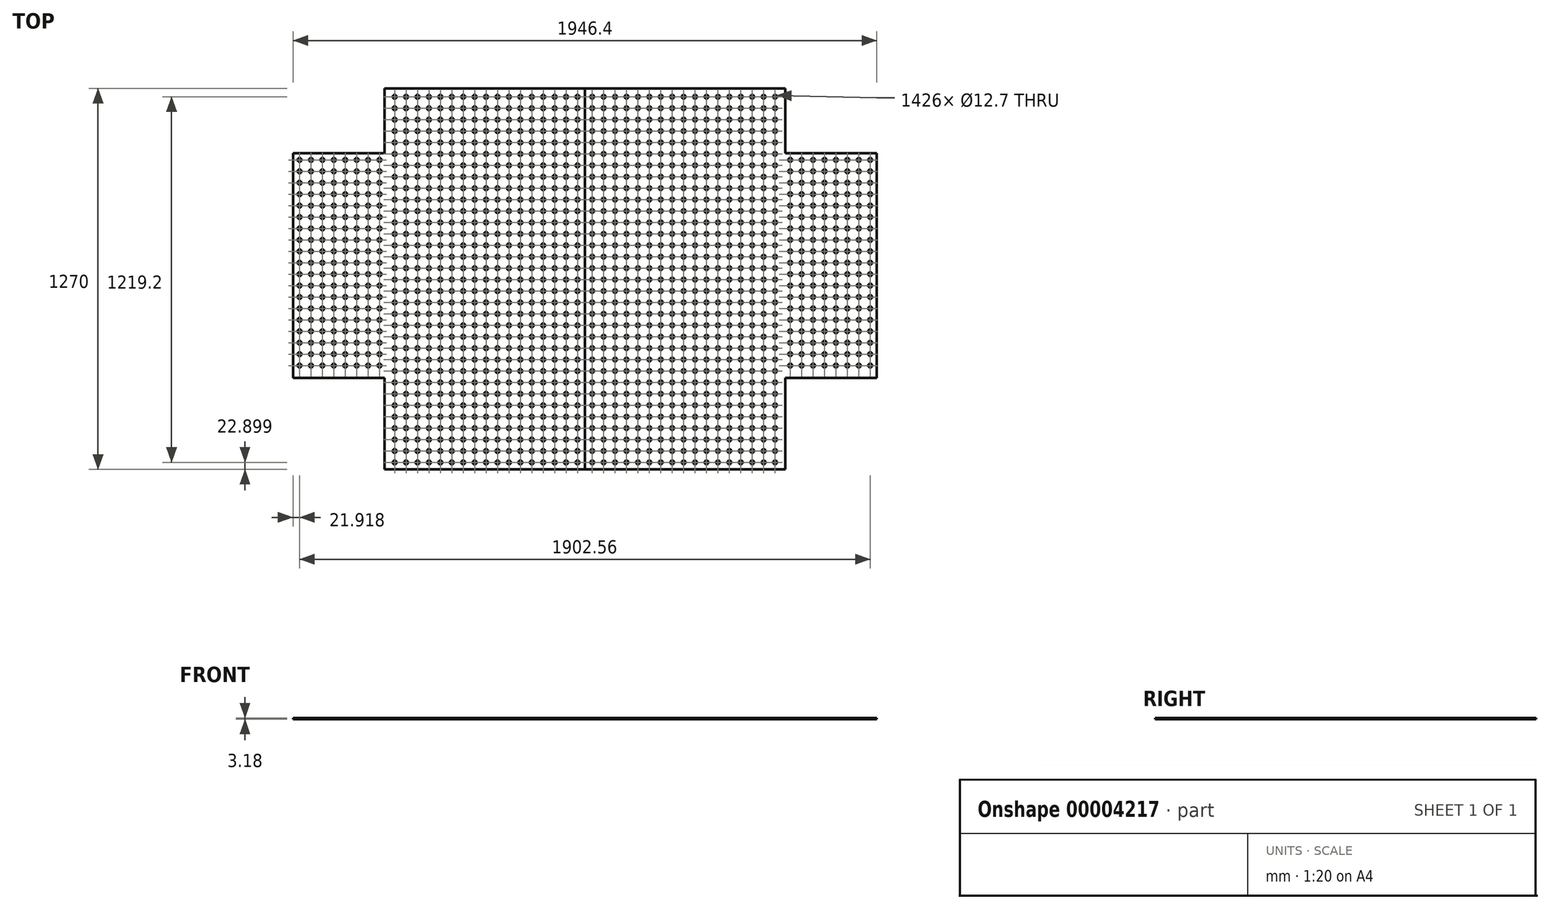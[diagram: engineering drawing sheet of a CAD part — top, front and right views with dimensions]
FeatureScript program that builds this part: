
annotation { "Feature Type Name" : "Feature", "Feature Type Description" : "" }
export const myFeature = defineFeature(function(context is Context, id is Id, definition is map)
    precondition{}
    {
        {
            var Q0;
            Q0=qCreatedBy(makeId("Top.planeOp"),FACE);
            var sketch = newSketch(context, id + "F0", { "sketchPlane" : qUnion([Q0])});
            skLineSegment(sketch, "E0.rect.bottom", {"start": v(-668.4, 635) * mm, "end": v(668.4, 635) * mm});
            skLineSegment(sketch, "E0.rect.top", {"start": v(-668.4, -635) * mm, "end": v(668.4, -635) * mm});
            skLineSegment(sketch, "E0.rect.left", {"start": v(-973.2, 419.1) * mm, "end": v(-973.2, -330.2) * mm});
            skLineSegment(sketch, "E0.rect.right", {"start": v(973.2, 419.1) * mm, "end": v(973.2, -330.2) * mm});
            skPoint(sketch, "E0.rect.middle", {"position": v(0, 0) * mm});
            skLineSegment(sketch, "E1.0", {"start": v(-973.2, 419.1) * mm, "end": v(-668.4, 419.1) * mm});
            skLineSegment(sketch, "E2.0", {"start": v(-973.2, -330.2) * mm, "end": v(-668.4, -330.2) * mm});
            skLineSegment(sketch, "E3.0", {"start": v(668.4, 635) * mm, "end": v(668.4, 419.1) * mm});
            skLineSegment(sketch, "E4.0", {"start": v(-668.4, 635) * mm, "end": v(-668.4, 419.1) * mm});
            skLineSegment(sketch, "E5.trimOffspring", {"start": v(668.4, 419.1) * mm, "end": v(973.2, 419.1) * mm});
            skLineSegment(sketch, "E6.trimOffspring", {"start": v(-668.4, -330.2) * mm, "end": v(-668.4, -635) * mm});
            skLineSegment(sketch, "E7.trimOffspring", {"start": v(668.4, -330.2) * mm, "end": v(973.2, -330.2) * mm});
            skLineSegment(sketch, "E8.trimOffspring", {"start": v(668.4, -330.2) * mm, "end": v(668.4, -635) * mm});
            skPoint(sketch, "E9.orphan", {"position": v(973.2, 635) * mm});
            skPoint(sketch, "E10.orphan", {"position": v(973.2, -635) * mm});
            skPoint(sketch, "E11.orphan", {"position": v(-973.2, -635) * mm});
            skPoint(sketch, "E12.orphan", {"position": v(-973.2, 635) * mm});
            skSolve(sketch);
        }
        {
            var Q0;
            Q0 = qSketchRegion(id + "F0", true);
            extrude(context, id + "F1", {"entities" : qUnion([Q0]), "depth" : 3.17 * mm});
        }
        {
            var Q0;
            Q0=makeQuery(id+"F1.opExtrude","CAP_FACE",FACE,{"disambiguationData":[OSD([sQuery(id+"F0.wireOp",EDGE,"E0.rect.bottom"),sQuery(id+"F0.wireOp",EDGE,"E0.rect.top"),sQuery(id+"F0.wireOp",EDGE,"E0.rect.left"),sQuery(id+"F0.wireOp",EDGE,"E0.rect.right"),sQuery(id+"F0.wireOp",EDGE,"E1.0"),sQuery(id+"F0.wireOp",EDGE,"E2.0"),sQuery(id+"F0.wireOp",EDGE,"E3.0"),sQuery(id+"F0.wireOp",EDGE,"E4.0"),sQuery(id+"F0.wireOp",EDGE,"E5.trimOffspring"),sQuery(id+"F0.wireOp",EDGE,"E6.trimOffspring"),sQuery(id+"F0.wireOp",EDGE,"E7.trimOffspring"),sQuery(id+"F0.wireOp",EDGE,"E8.trimOffspring")])],"isStart":false});
            var sketch = newSketch(context, id + "F2", { "sketchPlane" : qUnion([Q0])});
            skCircle(sketch, "E13", {"center": v(-634.04, 607.1) * mm, "radius": 6.35 * mm});
            skCircle(sketch, "E14.0.1.0", {"center": v(-634.04, 569) * mm, "radius": 6.35 * mm});
            skCircle(sketch, "E14.0.2.0", {"center": v(-634.04, 530.9) * mm, "radius": 6.35 * mm});
            skCircle(sketch, "E14.0.3.0", {"center": v(-634.04, 492.8) * mm, "radius": 6.35 * mm});
            skCircle(sketch, "E14.0.4.0", {"center": v(-634.04, 454.7) * mm, "radius": 6.35 * mm});
            skCircle(sketch, "E14.0.5.0", {"center": v(-634.04, 416.6) * mm, "radius": 6.35 * mm});
            skCircle(sketch, "E14.0.6.0", {"center": v(-634.04, 378.5) * mm, "radius": 6.35 * mm});
            skCircle(sketch, "E14.0.7.0", {"center": v(-634.04, 340.4) * mm, "radius": 6.35 * mm});
            skCircle(sketch, "E14.0.8.0", {"center": v(-634.04, 302.3) * mm, "radius": 6.35 * mm});
            skCircle(sketch, "E14.0.9.0", {"center": v(-634.04, 264.2) * mm, "radius": 6.35 * mm});
            skCircle(sketch, "E14.0.10.0", {"center": v(-634.04, 226.1) * mm, "radius": 6.35 * mm});
            skCircle(sketch, "E14.0.11.0", {"center": v(-634.04, 188) * mm, "radius": 6.35 * mm});
            skCircle(sketch, "E14.0.12.0", {"center": v(-634.04, 149.9) * mm, "radius": 6.35 * mm});
            skCircle(sketch, "E14.0.13.0", {"center": v(-634.04, 111.8) * mm, "radius": 6.35 * mm});
            skCircle(sketch, "E14.1.0.0", {"center": v(-595.94, 607.1) * mm, "radius": 6.35 * mm});
            skCircle(sketch, "E14.1.1.0", {"center": v(-595.94, 569) * mm, "radius": 6.35 * mm});
            skCircle(sketch, "E14.1.2.0", {"center": v(-595.94, 530.9) * mm, "radius": 6.35 * mm});
            skCircle(sketch, "E14.1.3.0", {"center": v(-595.94, 492.8) * mm, "radius": 6.35 * mm});
            skCircle(sketch, "E14.1.4.0", {"center": v(-595.94, 454.7) * mm, "radius": 6.35 * mm});
            skCircle(sketch, "E14.1.5.0", {"center": v(-595.94, 416.6) * mm, "radius": 6.35 * mm});
            skCircle(sketch, "E14.1.6.0", {"center": v(-595.94, 378.5) * mm, "radius": 6.35 * mm});
            skCircle(sketch, "E14.1.7.0", {"center": v(-595.94, 340.4) * mm, "radius": 6.35 * mm});
            skCircle(sketch, "E14.1.8.0", {"center": v(-595.94, 302.3) * mm, "radius": 6.35 * mm});
            skCircle(sketch, "E14.1.9.0", {"center": v(-595.94, 264.2) * mm, "radius": 6.35 * mm});
            skCircle(sketch, "E14.1.10.0", {"center": v(-595.94, 226.1) * mm, "radius": 6.35 * mm});
            skCircle(sketch, "E14.1.11.0", {"center": v(-595.94, 188) * mm, "radius": 6.35 * mm});
            skCircle(sketch, "E14.1.12.0", {"center": v(-595.94, 149.9) * mm, "radius": 6.35 * mm});
            skCircle(sketch, "E14.1.13.0", {"center": v(-595.94, 111.8) * mm, "radius": 6.35 * mm});
            skCircle(sketch, "E14.2.0.0", {"center": v(-557.84, 607.1) * mm, "radius": 6.35 * mm});
            skCircle(sketch, "E14.2.1.0", {"center": v(-557.84, 569) * mm, "radius": 6.35 * mm});
            skCircle(sketch, "E14.2.2.0", {"center": v(-557.84, 530.9) * mm, "radius": 6.35 * mm});
            skCircle(sketch, "E14.2.3.0", {"center": v(-557.84, 492.8) * mm, "radius": 6.35 * mm});
            skCircle(sketch, "E14.2.4.0", {"center": v(-557.84, 454.7) * mm, "radius": 6.35 * mm});
            skCircle(sketch, "E14.2.5.0", {"center": v(-557.84, 416.6) * mm, "radius": 6.35 * mm});
            skCircle(sketch, "E14.2.6.0", {"center": v(-557.84, 378.5) * mm, "radius": 6.35 * mm});
            skCircle(sketch, "E14.2.7.0", {"center": v(-557.84, 340.4) * mm, "radius": 6.35 * mm});
            skCircle(sketch, "E14.2.8.0", {"center": v(-557.84, 302.3) * mm, "radius": 6.35 * mm});
            skCircle(sketch, "E14.2.9.0", {"center": v(-557.84, 264.2) * mm, "radius": 6.35 * mm});
            skCircle(sketch, "E14.2.10.0", {"center": v(-557.84, 226.1) * mm, "radius": 6.35 * mm});
            skCircle(sketch, "E14.2.11.0", {"center": v(-557.84, 188) * mm, "radius": 6.35 * mm});
            skCircle(sketch, "E14.2.12.0", {"center": v(-557.84, 149.9) * mm, "radius": 6.35 * mm});
            skCircle(sketch, "E14.2.13.0", {"center": v(-557.84, 111.8) * mm, "radius": 6.35 * mm});
            skCircle(sketch, "E14.3.0.0", {"center": v(-519.74, 607.1) * mm, "radius": 6.35 * mm});
            skCircle(sketch, "E14.3.1.0", {"center": v(-519.74, 569) * mm, "radius": 6.35 * mm});
            skCircle(sketch, "E14.3.2.0", {"center": v(-519.74, 530.9) * mm, "radius": 6.35 * mm});
            skCircle(sketch, "E14.3.3.0", {"center": v(-519.74, 492.8) * mm, "radius": 6.35 * mm});
            skCircle(sketch, "E14.3.4.0", {"center": v(-519.74, 454.7) * mm, "radius": 6.35 * mm});
            skCircle(sketch, "E14.3.5.0", {"center": v(-519.74, 416.6) * mm, "radius": 6.35 * mm});
            skCircle(sketch, "E14.3.6.0", {"center": v(-519.74, 378.5) * mm, "radius": 6.35 * mm});
            skCircle(sketch, "E14.3.7.0", {"center": v(-519.74, 340.4) * mm, "radius": 6.35 * mm});
            skCircle(sketch, "E14.3.8.0", {"center": v(-519.74, 302.3) * mm, "radius": 6.35 * mm});
            skCircle(sketch, "E14.3.9.0", {"center": v(-519.74, 264.2) * mm, "radius": 6.35 * mm});
            skCircle(sketch, "E14.3.10.0", {"center": v(-519.74, 226.1) * mm, "radius": 6.35 * mm});
            skCircle(sketch, "E14.3.11.0", {"center": v(-519.74, 188) * mm, "radius": 6.35 * mm});
            skCircle(sketch, "E14.3.12.0", {"center": v(-519.74, 149.9) * mm, "radius": 6.35 * mm});
            skCircle(sketch, "E14.3.13.0", {"center": v(-519.74, 111.8) * mm, "radius": 6.35 * mm});
            skCircle(sketch, "E14.4.0.0", {"center": v(-481.64, 607.1) * mm, "radius": 6.35 * mm});
            skCircle(sketch, "E14.4.1.0", {"center": v(-481.64, 569) * mm, "radius": 6.35 * mm});
            skCircle(sketch, "E14.4.2.0", {"center": v(-481.64, 530.9) * mm, "radius": 6.35 * mm});
            skCircle(sketch, "E14.4.3.0", {"center": v(-481.64, 492.8) * mm, "radius": 6.35 * mm});
            skCircle(sketch, "E14.4.4.0", {"center": v(-481.64, 454.7) * mm, "radius": 6.35 * mm});
            skCircle(sketch, "E14.4.5.0", {"center": v(-481.64, 416.6) * mm, "radius": 6.35 * mm});
            skCircle(sketch, "E14.4.6.0", {"center": v(-481.64, 378.5) * mm, "radius": 6.35 * mm});
            skCircle(sketch, "E14.4.7.0", {"center": v(-481.64, 340.4) * mm, "radius": 6.35 * mm});
            skCircle(sketch, "E14.4.8.0", {"center": v(-481.64, 302.3) * mm, "radius": 6.35 * mm});
            skCircle(sketch, "E14.4.9.0", {"center": v(-481.64, 264.2) * mm, "radius": 6.35 * mm});
            skCircle(sketch, "E14.4.10.0", {"center": v(-481.64, 226.1) * mm, "radius": 6.35 * mm});
            skCircle(sketch, "E14.4.11.0", {"center": v(-481.64, 188) * mm, "radius": 6.35 * mm});
            skCircle(sketch, "E14.4.12.0", {"center": v(-481.64, 149.9) * mm, "radius": 6.35 * mm});
            skCircle(sketch, "E14.4.13.0", {"center": v(-481.64, 111.8) * mm, "radius": 6.35 * mm});
            skCircle(sketch, "E14.5.0.0", {"center": v(-443.54, 607.1) * mm, "radius": 6.35 * mm});
            skCircle(sketch, "E14.5.1.0", {"center": v(-443.54, 569) * mm, "radius": 6.35 * mm});
            skCircle(sketch, "E14.5.2.0", {"center": v(-443.54, 530.9) * mm, "radius": 6.35 * mm});
            skCircle(sketch, "E14.5.3.0", {"center": v(-443.54, 492.8) * mm, "radius": 6.35 * mm});
            skCircle(sketch, "E14.5.4.0", {"center": v(-443.54, 454.7) * mm, "radius": 6.35 * mm});
            skCircle(sketch, "E14.5.5.0", {"center": v(-443.54, 416.6) * mm, "radius": 6.35 * mm});
            skCircle(sketch, "E14.5.6.0", {"center": v(-443.54, 378.5) * mm, "radius": 6.35 * mm});
            skCircle(sketch, "E14.5.7.0", {"center": v(-443.54, 340.4) * mm, "radius": 6.35 * mm});
            skCircle(sketch, "E14.5.8.0", {"center": v(-443.54, 302.3) * mm, "radius": 6.35 * mm});
            skCircle(sketch, "E14.5.9.0", {"center": v(-443.54, 264.2) * mm, "radius": 6.35 * mm});
            skCircle(sketch, "E14.5.10.0", {"center": v(-443.54, 226.1) * mm, "radius": 6.35 * mm});
            skCircle(sketch, "E14.5.11.0", {"center": v(-443.54, 188) * mm, "radius": 6.35 * mm});
            skCircle(sketch, "E14.5.12.0", {"center": v(-443.54, 149.9) * mm, "radius": 6.35 * mm});
            skCircle(sketch, "E14.5.13.0", {"center": v(-443.54, 111.8) * mm, "radius": 6.35 * mm});
            skCircle(sketch, "E14.6.0.0", {"center": v(-405.44, 607.1) * mm, "radius": 6.35 * mm});
            skCircle(sketch, "E14.6.1.0", {"center": v(-405.44, 569) * mm, "radius": 6.35 * mm});
            skCircle(sketch, "E14.6.2.0", {"center": v(-405.44, 530.9) * mm, "radius": 6.35 * mm});
            skCircle(sketch, "E14.6.3.0", {"center": v(-405.44, 492.8) * mm, "radius": 6.35 * mm});
            skCircle(sketch, "E14.6.4.0", {"center": v(-405.44, 454.7) * mm, "radius": 6.35 * mm});
            skCircle(sketch, "E14.6.5.0", {"center": v(-405.44, 416.6) * mm, "radius": 6.35 * mm});
            skCircle(sketch, "E14.6.6.0", {"center": v(-405.44, 378.5) * mm, "radius": 6.35 * mm});
            skCircle(sketch, "E14.6.7.0", {"center": v(-405.44, 340.4) * mm, "radius": 6.35 * mm});
            skCircle(sketch, "E14.6.8.0", {"center": v(-405.44, 302.3) * mm, "radius": 6.35 * mm});
            skCircle(sketch, "E14.6.9.0", {"center": v(-405.44, 264.2) * mm, "radius": 6.35 * mm});
            skCircle(sketch, "E14.6.10.0", {"center": v(-405.44, 226.1) * mm, "radius": 6.35 * mm});
            skCircle(sketch, "E14.6.11.0", {"center": v(-405.44, 188) * mm, "radius": 6.35 * mm});
            skCircle(sketch, "E14.6.12.0", {"center": v(-405.44, 149.9) * mm, "radius": 6.35 * mm});
            skCircle(sketch, "E14.6.13.0", {"center": v(-405.44, 111.8) * mm, "radius": 6.35 * mm});
            skCircle(sketch, "E14.7.0.0", {"center": v(-367.34, 607.1) * mm, "radius": 6.35 * mm});
            skCircle(sketch, "E14.7.1.0", {"center": v(-367.34, 569) * mm, "radius": 6.35 * mm});
            skCircle(sketch, "E14.7.2.0", {"center": v(-367.34, 530.9) * mm, "radius": 6.35 * mm});
            skCircle(sketch, "E14.7.3.0", {"center": v(-367.34, 492.8) * mm, "radius": 6.35 * mm});
            skCircle(sketch, "E14.7.4.0", {"center": v(-367.34, 454.7) * mm, "radius": 6.35 * mm});
            skCircle(sketch, "E14.7.5.0", {"center": v(-367.34, 416.6) * mm, "radius": 6.35 * mm});
            skCircle(sketch, "E14.7.6.0", {"center": v(-367.34, 378.5) * mm, "radius": 6.35 * mm});
            skCircle(sketch, "E14.7.7.0", {"center": v(-367.34, 340.4) * mm, "radius": 6.35 * mm});
            skCircle(sketch, "E14.7.8.0", {"center": v(-367.34, 302.3) * mm, "radius": 6.35 * mm});
            skCircle(sketch, "E14.7.9.0", {"center": v(-367.34, 264.2) * mm, "radius": 6.35 * mm});
            skCircle(sketch, "E14.7.10.0", {"center": v(-367.34, 226.1) * mm, "radius": 6.35 * mm});
            skCircle(sketch, "E14.7.11.0", {"center": v(-367.34, 188) * mm, "radius": 6.35 * mm});
            skCircle(sketch, "E14.7.12.0", {"center": v(-367.34, 149.9) * mm, "radius": 6.35 * mm});
            skCircle(sketch, "E14.7.13.0", {"center": v(-367.34, 111.8) * mm, "radius": 6.35 * mm});
            skCircle(sketch, "E14.8.0.0", {"center": v(-329.24, 607.1) * mm, "radius": 6.35 * mm});
            skCircle(sketch, "E14.8.1.0", {"center": v(-329.24, 569) * mm, "radius": 6.35 * mm});
            skCircle(sketch, "E14.8.2.0", {"center": v(-329.24, 530.9) * mm, "radius": 6.35 * mm});
            skCircle(sketch, "E14.8.3.0", {"center": v(-329.24, 492.8) * mm, "radius": 6.35 * mm});
            skCircle(sketch, "E14.8.4.0", {"center": v(-329.24, 454.7) * mm, "radius": 6.35 * mm});
            skCircle(sketch, "E14.8.5.0", {"center": v(-329.24, 416.6) * mm, "radius": 6.35 * mm});
            skCircle(sketch, "E14.8.6.0", {"center": v(-329.24, 378.5) * mm, "radius": 6.35 * mm});
            skCircle(sketch, "E14.8.7.0", {"center": v(-329.24, 340.4) * mm, "radius": 6.35 * mm});
            skCircle(sketch, "E14.8.8.0", {"center": v(-329.24, 302.3) * mm, "radius": 6.35 * mm});
            skCircle(sketch, "E14.8.9.0", {"center": v(-329.24, 264.2) * mm, "radius": 6.35 * mm});
            skCircle(sketch, "E14.8.10.0", {"center": v(-329.24, 226.1) * mm, "radius": 6.35 * mm});
            skCircle(sketch, "E14.8.11.0", {"center": v(-329.24, 188) * mm, "radius": 6.35 * mm});
            skCircle(sketch, "E14.8.12.0", {"center": v(-329.24, 149.9) * mm, "radius": 6.35 * mm});
            skCircle(sketch, "E14.8.13.0", {"center": v(-329.24, 111.8) * mm, "radius": 6.35 * mm});
            skCircle(sketch, "E14.9.0.0", {"center": v(-291.14, 607.1) * mm, "radius": 6.35 * mm});
            skCircle(sketch, "E14.9.1.0", {"center": v(-291.14, 569) * mm, "radius": 6.35 * mm});
            skCircle(sketch, "E14.9.2.0", {"center": v(-291.14, 530.9) * mm, "radius": 6.35 * mm});
            skCircle(sketch, "E14.9.3.0", {"center": v(-291.14, 492.8) * mm, "radius": 6.35 * mm});
            skCircle(sketch, "E14.9.4.0", {"center": v(-291.14, 454.7) * mm, "radius": 6.35 * mm});
            skCircle(sketch, "E14.9.5.0", {"center": v(-291.14, 416.6) * mm, "radius": 6.35 * mm});
            skCircle(sketch, "E14.9.6.0", {"center": v(-291.14, 378.5) * mm, "radius": 6.35 * mm});
            skCircle(sketch, "E14.9.7.0", {"center": v(-291.14, 340.4) * mm, "radius": 6.35 * mm});
            skCircle(sketch, "E14.9.8.0", {"center": v(-291.14, 302.3) * mm, "radius": 6.35 * mm});
            skCircle(sketch, "E14.9.9.0", {"center": v(-291.14, 264.2) * mm, "radius": 6.35 * mm});
            skCircle(sketch, "E14.9.10.0", {"center": v(-291.14, 226.1) * mm, "radius": 6.35 * mm});
            skCircle(sketch, "E14.9.11.0", {"center": v(-291.14, 188) * mm, "radius": 6.35 * mm});
            skCircle(sketch, "E14.9.12.0", {"center": v(-291.14, 149.9) * mm, "radius": 6.35 * mm});
            skCircle(sketch, "E14.9.13.0", {"center": v(-291.14, 111.8) * mm, "radius": 6.35 * mm});
            skCircle(sketch, "E14.10.0.0", {"center": v(-253.04, 607.1) * mm, "radius": 6.35 * mm});
            skCircle(sketch, "E14.10.1.0", {"center": v(-253.04, 569) * mm, "radius": 6.35 * mm});
            skCircle(sketch, "E14.10.2.0", {"center": v(-253.04, 530.9) * mm, "radius": 6.35 * mm});
            skCircle(sketch, "E14.10.3.0", {"center": v(-253.04, 492.8) * mm, "radius": 6.35 * mm});
            skCircle(sketch, "E14.10.4.0", {"center": v(-253.04, 454.7) * mm, "radius": 6.35 * mm});
            skCircle(sketch, "E14.10.5.0", {"center": v(-253.04, 416.6) * mm, "radius": 6.35 * mm});
            skCircle(sketch, "E14.10.6.0", {"center": v(-253.04, 378.5) * mm, "radius": 6.35 * mm});
            skCircle(sketch, "E14.10.7.0", {"center": v(-253.04, 340.4) * mm, "radius": 6.35 * mm});
            skCircle(sketch, "E14.10.8.0", {"center": v(-253.04, 302.3) * mm, "radius": 6.35 * mm});
            skCircle(sketch, "E14.10.9.0", {"center": v(-253.04, 264.2) * mm, "radius": 6.35 * mm});
            skCircle(sketch, "E14.10.10.0", {"center": v(-253.04, 226.1) * mm, "radius": 6.35 * mm});
            skCircle(sketch, "E14.10.11.0", {"center": v(-253.04, 188) * mm, "radius": 6.35 * mm});
            skCircle(sketch, "E14.10.12.0", {"center": v(-253.04, 149.9) * mm, "radius": 6.35 * mm});
            skCircle(sketch, "E14.10.13.0", {"center": v(-253.04, 111.8) * mm, "radius": 6.35 * mm});
            skCircle(sketch, "E14.11.0.0", {"center": v(-214.94, 607.1) * mm, "radius": 6.35 * mm});
            skCircle(sketch, "E14.11.1.0", {"center": v(-214.94, 569) * mm, "radius": 6.35 * mm});
            skCircle(sketch, "E14.11.2.0", {"center": v(-214.94, 530.9) * mm, "radius": 6.35 * mm});
            skCircle(sketch, "E14.11.3.0", {"center": v(-214.94, 492.8) * mm, "radius": 6.35 * mm});
            skCircle(sketch, "E14.11.4.0", {"center": v(-214.94, 454.7) * mm, "radius": 6.35 * mm});
            skCircle(sketch, "E14.11.5.0", {"center": v(-214.94, 416.6) * mm, "radius": 6.35 * mm});
            skCircle(sketch, "E14.11.6.0", {"center": v(-214.94, 378.5) * mm, "radius": 6.35 * mm});
            skCircle(sketch, "E14.11.7.0", {"center": v(-214.94, 340.4) * mm, "radius": 6.35 * mm});
            skCircle(sketch, "E14.11.8.0", {"center": v(-214.94, 302.3) * mm, "radius": 6.35 * mm});
            skCircle(sketch, "E14.11.9.0", {"center": v(-214.94, 264.2) * mm, "radius": 6.35 * mm});
            skCircle(sketch, "E14.11.10.0", {"center": v(-214.94, 226.1) * mm, "radius": 6.35 * mm});
            skCircle(sketch, "E14.11.11.0", {"center": v(-214.94, 188) * mm, "radius": 6.35 * mm});
            skCircle(sketch, "E14.11.12.0", {"center": v(-214.94, 149.9) * mm, "radius": 6.35 * mm});
            skCircle(sketch, "E14.11.13.0", {"center": v(-214.94, 111.8) * mm, "radius": 6.35 * mm});
            skCircle(sketch, "E14.12.0.0", {"center": v(-176.84, 607.1) * mm, "radius": 6.35 * mm});
            skCircle(sketch, "E14.12.1.0", {"center": v(-176.84, 569) * mm, "radius": 6.35 * mm});
            skCircle(sketch, "E14.12.2.0", {"center": v(-176.84, 530.9) * mm, "radius": 6.35 * mm});
            skCircle(sketch, "E14.12.3.0", {"center": v(-176.84, 492.8) * mm, "radius": 6.35 * mm});
            skCircle(sketch, "E14.12.4.0", {"center": v(-176.84, 454.7) * mm, "radius": 6.35 * mm});
            skCircle(sketch, "E14.12.5.0", {"center": v(-176.84, 416.6) * mm, "radius": 6.35 * mm});
            skCircle(sketch, "E14.12.6.0", {"center": v(-176.84, 378.5) * mm, "radius": 6.35 * mm});
            skCircle(sketch, "E14.12.7.0", {"center": v(-176.84, 340.4) * mm, "radius": 6.35 * mm});
            skCircle(sketch, "E14.12.8.0", {"center": v(-176.84, 302.3) * mm, "radius": 6.35 * mm});
            skCircle(sketch, "E14.12.9.0", {"center": v(-176.84, 264.2) * mm, "radius": 6.35 * mm});
            skCircle(sketch, "E14.12.10.0", {"center": v(-176.84, 226.1) * mm, "radius": 6.35 * mm});
            skCircle(sketch, "E14.12.11.0", {"center": v(-176.84, 188) * mm, "radius": 6.35 * mm});
            skCircle(sketch, "E14.12.12.0", {"center": v(-176.84, 149.9) * mm, "radius": 6.35 * mm});
            skCircle(sketch, "E14.12.13.0", {"center": v(-176.84, 111.8) * mm, "radius": 6.35 * mm});
            skCircle(sketch, "E14.13.0.0", {"center": v(-138.74, 607.1) * mm, "radius": 6.35 * mm});
            skCircle(sketch, "E14.13.1.0", {"center": v(-138.74, 569) * mm, "radius": 6.35 * mm});
            skCircle(sketch, "E14.13.2.0", {"center": v(-138.74, 530.9) * mm, "radius": 6.35 * mm});
            skCircle(sketch, "E14.13.3.0", {"center": v(-138.74, 492.8) * mm, "radius": 6.35 * mm});
            skCircle(sketch, "E14.13.4.0", {"center": v(-138.74, 454.7) * mm, "radius": 6.35 * mm});
            skCircle(sketch, "E14.13.5.0", {"center": v(-138.74, 416.6) * mm, "radius": 6.35 * mm});
            skCircle(sketch, "E14.13.6.0", {"center": v(-138.74, 378.5) * mm, "radius": 6.35 * mm});
            skCircle(sketch, "E14.13.7.0", {"center": v(-138.74, 340.4) * mm, "radius": 6.35 * mm});
            skCircle(sketch, "E14.13.8.0", {"center": v(-138.74, 302.3) * mm, "radius": 6.35 * mm});
            skCircle(sketch, "E14.13.9.0", {"center": v(-138.74, 264.2) * mm, "radius": 6.35 * mm});
            skCircle(sketch, "E14.13.10.0", {"center": v(-138.74, 226.1) * mm, "radius": 6.35 * mm});
            skCircle(sketch, "E14.13.11.0", {"center": v(-138.74, 188) * mm, "radius": 6.35 * mm});
            skCircle(sketch, "E14.13.12.0", {"center": v(-138.74, 149.9) * mm, "radius": 6.35 * mm});
            skCircle(sketch, "E14.13.13.0", {"center": v(-138.74, 111.8) * mm, "radius": 6.35 * mm});
            skCircle(sketch, "E14.14.0.0", {"center": v(-100.64, 607.1) * mm, "radius": 6.35 * mm});
            skCircle(sketch, "E14.14.1.0", {"center": v(-100.64, 569) * mm, "radius": 6.35 * mm});
            skCircle(sketch, "E14.14.2.0", {"center": v(-100.64, 530.9) * mm, "radius": 6.35 * mm});
            skCircle(sketch, "E14.14.3.0", {"center": v(-100.64, 492.8) * mm, "radius": 6.35 * mm});
            skCircle(sketch, "E14.14.4.0", {"center": v(-100.64, 454.7) * mm, "radius": 6.35 * mm});
            skCircle(sketch, "E14.14.5.0", {"center": v(-100.64, 416.6) * mm, "radius": 6.35 * mm});
            skCircle(sketch, "E14.14.6.0", {"center": v(-100.64, 378.5) * mm, "radius": 6.35 * mm});
            skCircle(sketch, "E14.14.7.0", {"center": v(-100.64, 340.4) * mm, "radius": 6.35 * mm});
            skCircle(sketch, "E14.14.8.0", {"center": v(-100.64, 302.3) * mm, "radius": 6.35 * mm});
            skCircle(sketch, "E14.14.9.0", {"center": v(-100.64, 264.2) * mm, "radius": 6.35 * mm});
            skCircle(sketch, "E14.14.10.0", {"center": v(-100.64, 226.1) * mm, "radius": 6.35 * mm});
            skCircle(sketch, "E14.14.11.0", {"center": v(-100.64, 188) * mm, "radius": 6.35 * mm});
            skCircle(sketch, "E14.14.12.0", {"center": v(-100.64, 149.9) * mm, "radius": 6.35 * mm});
            skCircle(sketch, "E14.14.13.0", {"center": v(-100.64, 111.8) * mm, "radius": 6.35 * mm});
            skCircle(sketch, "E14.15.0.0", {"center": v(-62.54, 607.1) * mm, "radius": 6.35 * mm});
            skCircle(sketch, "E14.15.1.0", {"center": v(-62.54, 569) * mm, "radius": 6.35 * mm});
            skCircle(sketch, "E14.15.2.0", {"center": v(-62.54, 530.9) * mm, "radius": 6.35 * mm});
            skCircle(sketch, "E14.15.3.0", {"center": v(-62.54, 492.8) * mm, "radius": 6.35 * mm});
            skCircle(sketch, "E14.15.4.0", {"center": v(-62.54, 454.7) * mm, "radius": 6.35 * mm});
            skCircle(sketch, "E14.15.5.0", {"center": v(-62.54, 416.6) * mm, "radius": 6.35 * mm});
            skCircle(sketch, "E14.15.6.0", {"center": v(-62.54, 378.5) * mm, "radius": 6.35 * mm});
            skCircle(sketch, "E14.15.7.0", {"center": v(-62.54, 340.4) * mm, "radius": 6.35 * mm});
            skCircle(sketch, "E14.15.8.0", {"center": v(-62.54, 302.3) * mm, "radius": 6.35 * mm});
            skCircle(sketch, "E14.15.9.0", {"center": v(-62.54, 264.2) * mm, "radius": 6.35 * mm});
            skCircle(sketch, "E14.15.10.0", {"center": v(-62.54, 226.1) * mm, "radius": 6.35 * mm});
            skCircle(sketch, "E14.15.11.0", {"center": v(-62.54, 188) * mm, "radius": 6.35 * mm});
            skCircle(sketch, "E14.15.12.0", {"center": v(-62.54, 149.9) * mm, "radius": 6.35 * mm});
            skCircle(sketch, "E14.15.13.0", {"center": v(-62.54, 111.8) * mm, "radius": 6.35 * mm});
            skCircle(sketch, "E14.16.0.0", {"center": v(-24.44, 607.1) * mm, "radius": 6.35 * mm});
            skCircle(sketch, "E14.16.1.0", {"center": v(-24.44, 569) * mm, "radius": 6.35 * mm});
            skCircle(sketch, "E14.16.2.0", {"center": v(-24.44, 530.9) * mm, "radius": 6.35 * mm});
            skCircle(sketch, "E14.16.3.0", {"center": v(-24.44, 492.8) * mm, "radius": 6.35 * mm});
            skCircle(sketch, "E14.16.4.0", {"center": v(-24.44, 454.7) * mm, "radius": 6.35 * mm});
            skCircle(sketch, "E14.16.5.0", {"center": v(-24.44, 416.6) * mm, "radius": 6.35 * mm});
            skCircle(sketch, "E14.16.6.0", {"center": v(-24.44, 378.5) * mm, "radius": 6.35 * mm});
            skCircle(sketch, "E14.16.7.0", {"center": v(-24.44, 340.4) * mm, "radius": 6.35 * mm});
            skCircle(sketch, "E14.16.8.0", {"center": v(-24.44, 302.3) * mm, "radius": 6.35 * mm});
            skCircle(sketch, "E14.16.9.0", {"center": v(-24.44, 264.2) * mm, "radius": 6.35 * mm});
            skCircle(sketch, "E14.16.10.0", {"center": v(-24.44, 226.1) * mm, "radius": 6.35 * mm});
            skCircle(sketch, "E14.16.11.0", {"center": v(-24.44, 188) * mm, "radius": 6.35 * mm});
            skCircle(sketch, "E14.16.12.0", {"center": v(-24.44, 149.9) * mm, "radius": 6.35 * mm});
            skCircle(sketch, "E14.16.13.0", {"center": v(-24.44, 111.8) * mm, "radius": 6.35 * mm});
            skCircle(sketch, "E14.17.0.0", {"center": v(13.66, 607.1) * mm, "radius": 6.35 * mm});
            skCircle(sketch, "E14.17.1.0", {"center": v(13.66, 569) * mm, "radius": 6.35 * mm});
            skCircle(sketch, "E14.17.2.0", {"center": v(13.66, 530.9) * mm, "radius": 6.35 * mm});
            skCircle(sketch, "E14.17.3.0", {"center": v(13.66, 492.8) * mm, "radius": 6.35 * mm});
            skCircle(sketch, "E14.17.4.0", {"center": v(13.66, 454.7) * mm, "radius": 6.35 * mm});
            skCircle(sketch, "E14.17.5.0", {"center": v(13.66, 416.6) * mm, "radius": 6.35 * mm});
            skCircle(sketch, "E14.17.6.0", {"center": v(13.66, 378.5) * mm, "radius": 6.35 * mm});
            skCircle(sketch, "E14.17.7.0", {"center": v(13.66, 340.4) * mm, "radius": 6.35 * mm});
            skCircle(sketch, "E14.17.8.0", {"center": v(13.66, 302.3) * mm, "radius": 6.35 * mm});
            skCircle(sketch, "E14.17.9.0", {"center": v(13.66, 264.2) * mm, "radius": 6.35 * mm});
            skCircle(sketch, "E14.17.10.0", {"center": v(13.66, 226.1) * mm, "radius": 6.35 * mm});
            skCircle(sketch, "E14.17.11.0", {"center": v(13.66, 188) * mm, "radius": 6.35 * mm});
            skCircle(sketch, "E14.17.12.0", {"center": v(13.66, 149.9) * mm, "radius": 6.35 * mm});
            skCircle(sketch, "E14.17.13.0", {"center": v(13.66, 111.8) * mm, "radius": 6.35 * mm});
            skLineSegment(sketch, "E14.direction1", {"start": v(-634.04, 607.1) * mm, "end": v(-595.94, 607.1) * mm, "construction": true});
            skLineSegment(sketch, "E14.direction2", {"start": v(-634.04, 607.1) * mm, "end": v(-634.04, 569) * mm, "construction": true});
            skSolve(sketch);
        }
        {
            var Q0;
            Q0 = qSketchRegion(id + "F2", true);
            extrude(context, id + "F3", {"entities" : qUnion([Q0]), "operationType" : NewBodyOperationType.REMOVE, "endBound" : BoundingType.THROUGH_ALL, "oppositeDirection" : true, "depth" : 25.4 * mm});
        }
        {
            var Q0;
            Q0=makeQuery(id+"F1.opExtrude","CAP_FACE",FACE,{"disambiguationData":[OSD([sQuery(id+"F0.wireOp",EDGE,"E0.rect.bottom"),sQuery(id+"F0.wireOp",EDGE,"E0.rect.top"),sQuery(id+"F0.wireOp",EDGE,"E0.rect.left"),sQuery(id+"F0.wireOp",EDGE,"E0.rect.right"),sQuery(id+"F0.wireOp",EDGE,"E1.0"),sQuery(id+"F0.wireOp",EDGE,"E2.0"),sQuery(id+"F0.wireOp",EDGE,"E3.0"),sQuery(id+"F0.wireOp",EDGE,"E4.0"),sQuery(id+"F0.wireOp",EDGE,"E5.trimOffspring"),sQuery(id+"F0.wireOp",EDGE,"E6.trimOffspring"),sQuery(id+"F0.wireOp",EDGE,"E7.trimOffspring"),sQuery(id+"F0.wireOp",EDGE,"E8.trimOffspring")])],"isStart":false});
            var sketch = newSketch(context, id + "F4", { "sketchPlane" : qUnion([Q0])});
            skCircle(sketch, "E15", {"center": v(-951.28, 396.59) * mm, "radius": 6.35 * mm});
            skCircle(sketch, "E16.0.1.0", {"center": v(-951.28, 358.49) * mm, "radius": 6.35 * mm});
            skCircle(sketch, "E16.0.2.0", {"center": v(-951.28, 320.39) * mm, "radius": 6.35 * mm});
            skCircle(sketch, "E16.0.3.0", {"center": v(-951.28, 282.29) * mm, "radius": 6.35 * mm});
            skCircle(sketch, "E16.0.4.0", {"center": v(-951.28, 244.19) * mm, "radius": 6.35 * mm});
            skCircle(sketch, "E16.0.5.0", {"center": v(-951.28, 206.09) * mm, "radius": 6.35 * mm});
            skCircle(sketch, "E16.0.6.0", {"center": v(-951.28, 167.99) * mm, "radius": 6.35 * mm});
            skCircle(sketch, "E16.0.7.0", {"center": v(-951.28, 129.89) * mm, "radius": 6.35 * mm});
            skCircle(sketch, "E16.0.8.0", {"center": v(-951.28, 91.79) * mm, "radius": 6.35 * mm});
            skCircle(sketch, "E16.0.9.0", {"center": v(-951.28, 53.69) * mm, "radius": 6.35 * mm});
            skCircle(sketch, "E16.0.10.0", {"center": v(-951.28, 15.59) * mm, "radius": 6.35 * mm});
            skCircle(sketch, "E16.0.11.0", {"center": v(-951.28, -22.51) * mm, "radius": 6.35 * mm});
            skCircle(sketch, "E16.1.0.0", {"center": v(-913.18, 396.59) * mm, "radius": 6.35 * mm});
            skCircle(sketch, "E16.1.1.0", {"center": v(-913.18, 358.49) * mm, "radius": 6.35 * mm});
            skCircle(sketch, "E16.1.2.0", {"center": v(-913.18, 320.39) * mm, "radius": 6.35 * mm});
            skCircle(sketch, "E16.1.3.0", {"center": v(-913.18, 282.29) * mm, "radius": 6.35 * mm});
            skCircle(sketch, "E16.1.4.0", {"center": v(-913.18, 244.19) * mm, "radius": 6.35 * mm});
            skCircle(sketch, "E16.1.5.0", {"center": v(-913.18, 206.09) * mm, "radius": 6.35 * mm});
            skCircle(sketch, "E16.1.6.0", {"center": v(-913.18, 167.99) * mm, "radius": 6.35 * mm});
            skCircle(sketch, "E16.1.7.0", {"center": v(-913.18, 129.89) * mm, "radius": 6.35 * mm});
            skCircle(sketch, "E16.1.8.0", {"center": v(-913.18, 91.79) * mm, "radius": 6.35 * mm});
            skCircle(sketch, "E16.1.9.0", {"center": v(-913.18, 53.69) * mm, "radius": 6.35 * mm});
            skCircle(sketch, "E16.1.10.0", {"center": v(-913.18, 15.59) * mm, "radius": 6.35 * mm});
            skCircle(sketch, "E16.1.11.0", {"center": v(-913.18, -22.51) * mm, "radius": 6.35 * mm});
            skCircle(sketch, "E16.2.0.0", {"center": v(-875.08, 396.59) * mm, "radius": 6.35 * mm});
            skCircle(sketch, "E16.2.1.0", {"center": v(-875.08, 358.49) * mm, "radius": 6.35 * mm});
            skCircle(sketch, "E16.2.2.0", {"center": v(-875.08, 320.39) * mm, "radius": 6.35 * mm});
            skCircle(sketch, "E16.2.3.0", {"center": v(-875.08, 282.29) * mm, "radius": 6.35 * mm});
            skCircle(sketch, "E16.2.4.0", {"center": v(-875.08, 244.19) * mm, "radius": 6.35 * mm});
            skCircle(sketch, "E16.2.5.0", {"center": v(-875.08, 206.09) * mm, "radius": 6.35 * mm});
            skCircle(sketch, "E16.2.6.0", {"center": v(-875.08, 167.99) * mm, "radius": 6.35 * mm});
            skCircle(sketch, "E16.2.7.0", {"center": v(-875.08, 129.89) * mm, "radius": 6.35 * mm});
            skCircle(sketch, "E16.2.8.0", {"center": v(-875.08, 91.79) * mm, "radius": 6.35 * mm});
            skCircle(sketch, "E16.2.9.0", {"center": v(-875.08, 53.69) * mm, "radius": 6.35 * mm});
            skCircle(sketch, "E16.2.10.0", {"center": v(-875.08, 15.59) * mm, "radius": 6.35 * mm});
            skCircle(sketch, "E16.2.11.0", {"center": v(-875.08, -22.51) * mm, "radius": 6.35 * mm});
            skCircle(sketch, "E16.3.0.0", {"center": v(-836.98, 396.59) * mm, "radius": 6.35 * mm});
            skCircle(sketch, "E16.3.1.0", {"center": v(-836.98, 358.49) * mm, "radius": 6.35 * mm});
            skCircle(sketch, "E16.3.2.0", {"center": v(-836.98, 320.39) * mm, "radius": 6.35 * mm});
            skCircle(sketch, "E16.3.3.0", {"center": v(-836.98, 282.29) * mm, "radius": 6.35 * mm});
            skCircle(sketch, "E16.3.4.0", {"center": v(-836.98, 244.19) * mm, "radius": 6.35 * mm});
            skCircle(sketch, "E16.3.5.0", {"center": v(-836.98, 206.09) * mm, "radius": 6.35 * mm});
            skCircle(sketch, "E16.3.6.0", {"center": v(-836.98, 167.99) * mm, "radius": 6.35 * mm});
            skCircle(sketch, "E16.3.7.0", {"center": v(-836.98, 129.89) * mm, "radius": 6.35 * mm});
            skCircle(sketch, "E16.3.8.0", {"center": v(-836.98, 91.79) * mm, "radius": 6.35 * mm});
            skCircle(sketch, "E16.3.9.0", {"center": v(-836.98, 53.69) * mm, "radius": 6.35 * mm});
            skCircle(sketch, "E16.3.10.0", {"center": v(-836.98, 15.59) * mm, "radius": 6.35 * mm});
            skCircle(sketch, "E16.3.11.0", {"center": v(-836.98, -22.51) * mm, "radius": 6.35 * mm});
            skCircle(sketch, "E16.4.0.0", {"center": v(-798.88, 396.59) * mm, "radius": 6.35 * mm});
            skCircle(sketch, "E16.4.1.0", {"center": v(-798.88, 358.49) * mm, "radius": 6.35 * mm});
            skCircle(sketch, "E16.4.2.0", {"center": v(-798.88, 320.39) * mm, "radius": 6.35 * mm});
            skCircle(sketch, "E16.4.3.0", {"center": v(-798.88, 282.29) * mm, "radius": 6.35 * mm});
            skCircle(sketch, "E16.4.4.0", {"center": v(-798.88, 244.19) * mm, "radius": 6.35 * mm});
            skCircle(sketch, "E16.4.5.0", {"center": v(-798.88, 206.09) * mm, "radius": 6.35 * mm});
            skCircle(sketch, "E16.4.6.0", {"center": v(-798.88, 167.99) * mm, "radius": 6.35 * mm});
            skCircle(sketch, "E16.4.7.0", {"center": v(-798.88, 129.89) * mm, "radius": 6.35 * mm});
            skCircle(sketch, "E16.4.8.0", {"center": v(-798.88, 91.79) * mm, "radius": 6.35 * mm});
            skCircle(sketch, "E16.4.9.0", {"center": v(-798.88, 53.69) * mm, "radius": 6.35 * mm});
            skCircle(sketch, "E16.4.10.0", {"center": v(-798.88, 15.59) * mm, "radius": 6.35 * mm});
            skCircle(sketch, "E16.4.11.0", {"center": v(-798.88, -22.51) * mm, "radius": 6.35 * mm});
            skCircle(sketch, "E16.5.0.0", {"center": v(-760.78, 396.59) * mm, "radius": 6.35 * mm});
            skCircle(sketch, "E16.5.1.0", {"center": v(-760.78, 358.49) * mm, "radius": 6.35 * mm});
            skCircle(sketch, "E16.5.2.0", {"center": v(-760.78, 320.39) * mm, "radius": 6.35 * mm});
            skCircle(sketch, "E16.5.3.0", {"center": v(-760.78, 282.29) * mm, "radius": 6.35 * mm});
            skCircle(sketch, "E16.5.4.0", {"center": v(-760.78, 244.19) * mm, "radius": 6.35 * mm});
            skCircle(sketch, "E16.5.5.0", {"center": v(-760.78, 206.09) * mm, "radius": 6.35 * mm});
            skCircle(sketch, "E16.5.6.0", {"center": v(-760.78, 167.99) * mm, "radius": 6.35 * mm});
            skCircle(sketch, "E16.5.7.0", {"center": v(-760.78, 129.89) * mm, "radius": 6.35 * mm});
            skCircle(sketch, "E16.5.8.0", {"center": v(-760.78, 91.79) * mm, "radius": 6.35 * mm});
            skCircle(sketch, "E16.5.9.0", {"center": v(-760.78, 53.69) * mm, "radius": 6.35 * mm});
            skCircle(sketch, "E16.5.10.0", {"center": v(-760.78, 15.59) * mm, "radius": 6.35 * mm});
            skCircle(sketch, "E16.5.11.0", {"center": v(-760.78, -22.51) * mm, "radius": 6.35 * mm});
            skCircle(sketch, "E16.6.0.0", {"center": v(-722.68, 396.59) * mm, "radius": 6.35 * mm});
            skCircle(sketch, "E16.6.1.0", {"center": v(-722.68, 358.49) * mm, "radius": 6.35 * mm});
            skCircle(sketch, "E16.6.2.0", {"center": v(-722.68, 320.39) * mm, "radius": 6.35 * mm});
            skCircle(sketch, "E16.6.3.0", {"center": v(-722.68, 282.29) * mm, "radius": 6.35 * mm});
            skCircle(sketch, "E16.6.4.0", {"center": v(-722.68, 244.19) * mm, "radius": 6.35 * mm});
            skCircle(sketch, "E16.6.5.0", {"center": v(-722.68, 206.09) * mm, "radius": 6.35 * mm});
            skCircle(sketch, "E16.6.6.0", {"center": v(-722.68, 167.99) * mm, "radius": 6.35 * mm});
            skCircle(sketch, "E16.6.7.0", {"center": v(-722.68, 129.89) * mm, "radius": 6.35 * mm});
            skCircle(sketch, "E16.6.8.0", {"center": v(-722.68, 91.79) * mm, "radius": 6.35 * mm});
            skCircle(sketch, "E16.6.9.0", {"center": v(-722.68, 53.69) * mm, "radius": 6.35 * mm});
            skCircle(sketch, "E16.6.10.0", {"center": v(-722.68, 15.59) * mm, "radius": 6.35 * mm});
            skCircle(sketch, "E16.6.11.0", {"center": v(-722.68, -22.51) * mm, "radius": 6.35 * mm});
            skCircle(sketch, "E16.7.0.0", {"center": v(-684.58, 396.59) * mm, "radius": 6.35 * mm});
            skCircle(sketch, "E16.7.1.0", {"center": v(-684.58, 358.49) * mm, "radius": 6.35 * mm});
            skCircle(sketch, "E16.7.2.0", {"center": v(-684.58, 320.39) * mm, "radius": 6.35 * mm});
            skCircle(sketch, "E16.7.3.0", {"center": v(-684.58, 282.29) * mm, "radius": 6.35 * mm});
            skCircle(sketch, "E16.7.4.0", {"center": v(-684.58, 244.19) * mm, "radius": 6.35 * mm});
            skCircle(sketch, "E16.7.5.0", {"center": v(-684.58, 206.09) * mm, "radius": 6.35 * mm});
            skCircle(sketch, "E16.7.6.0", {"center": v(-684.58, 167.99) * mm, "radius": 6.35 * mm});
            skCircle(sketch, "E16.7.7.0", {"center": v(-684.58, 129.89) * mm, "radius": 6.35 * mm});
            skCircle(sketch, "E16.7.8.0", {"center": v(-684.58, 91.79) * mm, "radius": 6.35 * mm});
            skCircle(sketch, "E16.7.9.0", {"center": v(-684.58, 53.69) * mm, "radius": 6.35 * mm});
            skCircle(sketch, "E16.7.10.0", {"center": v(-684.58, 15.59) * mm, "radius": 6.35 * mm});
            skCircle(sketch, "E16.7.11.0", {"center": v(-684.58, -22.51) * mm, "radius": 6.35 * mm});
            skLineSegment(sketch, "E16.direction1", {"start": v(-951.28, 396.59) * mm, "end": v(-913.18, 396.59) * mm, "construction": true});
            skLineSegment(sketch, "E16.direction2", {"start": v(-951.28, 396.59) * mm, "end": v(-951.28, 358.49) * mm, "construction": true});
            skSolve(sketch);
        }
        {
            var Q0;
            Q0 = qSketchRegion(id + "F4", true);
            extrude(context, id + "F5", {"entities" : qUnion([Q0]), "operationType" : NewBodyOperationType.REMOVE, "endBound" : BoundingType.THROUGH_ALL, "oppositeDirection" : true, "depth" : 25.4 * mm});
        }
        {
            var Q0;
            Q0=makeQuery(id+"F1.opExtrude","CAP_FACE",FACE,{"disambiguationData":[OSD([sQuery(id+"F0.wireOp",EDGE,"E0.rect.bottom"),sQuery(id+"F0.wireOp",EDGE,"E0.rect.top"),sQuery(id+"F0.wireOp",EDGE,"E0.rect.left"),sQuery(id+"F0.wireOp",EDGE,"E0.rect.right"),sQuery(id+"F0.wireOp",EDGE,"E1.0"),sQuery(id+"F0.wireOp",EDGE,"E2.0"),sQuery(id+"F0.wireOp",EDGE,"E3.0"),sQuery(id+"F0.wireOp",EDGE,"E4.0"),sQuery(id+"F0.wireOp",EDGE,"E5.trimOffspring"),sQuery(id+"F0.wireOp",EDGE,"E6.trimOffspring"),sQuery(id+"F0.wireOp",EDGE,"E7.trimOffspring"),sQuery(id+"F0.wireOp",EDGE,"E8.trimOffspring")])],"isStart":false});
            var sketch = newSketch(context, id + "F6", { "sketchPlane" : qUnion([Q0])});
            skCircle(sketch, "E17.0", {"center": v(-951.28, -22.51) * mm, "radius": 6.35 * mm});
            skCircle(sketch, "E18.0.1.0", {"center": v(-951.28, -60.61) * mm, "radius": 6.35 * mm});
            skCircle(sketch, "E18.0.2.0", {"center": v(-951.28, -98.71) * mm, "radius": 6.35 * mm});
            skCircle(sketch, "E18.0.3.0", {"center": v(-951.28, -136.81) * mm, "radius": 6.35 * mm});
            skCircle(sketch, "E18.0.4.0", {"center": v(-951.28, -174.91) * mm, "radius": 6.35 * mm});
            skCircle(sketch, "E18.0.5.0", {"center": v(-951.28, -213.01) * mm, "radius": 6.35 * mm});
            skCircle(sketch, "E18.0.6.0", {"center": v(-951.28, -251.11) * mm, "radius": 6.35 * mm});
            skCircle(sketch, "E18.0.7.0", {"center": v(-951.28, -289.21) * mm, "radius": 6.35 * mm});
            skCircle(sketch, "E18.1.0.0", {"center": v(-913.18, -22.51) * mm, "radius": 6.35 * mm});
            skCircle(sketch, "E18.1.1.0", {"center": v(-913.18, -60.61) * mm, "radius": 6.35 * mm});
            skCircle(sketch, "E18.1.2.0", {"center": v(-913.18, -98.71) * mm, "radius": 6.35 * mm});
            skCircle(sketch, "E18.1.3.0", {"center": v(-913.18, -136.81) * mm, "radius": 6.35 * mm});
            skCircle(sketch, "E18.1.4.0", {"center": v(-913.18, -174.91) * mm, "radius": 6.35 * mm});
            skCircle(sketch, "E18.1.5.0", {"center": v(-913.18, -213.01) * mm, "radius": 6.35 * mm});
            skCircle(sketch, "E18.1.6.0", {"center": v(-913.18, -251.11) * mm, "radius": 6.35 * mm});
            skCircle(sketch, "E18.1.7.0", {"center": v(-913.18, -289.21) * mm, "radius": 6.35 * mm});
            skCircle(sketch, "E18.2.0.0", {"center": v(-875.08, -22.51) * mm, "radius": 6.35 * mm});
            skCircle(sketch, "E18.2.1.0", {"center": v(-875.08, -60.61) * mm, "radius": 6.35 * mm});
            skCircle(sketch, "E18.2.2.0", {"center": v(-875.08, -98.71) * mm, "radius": 6.35 * mm});
            skCircle(sketch, "E18.2.3.0", {"center": v(-875.08, -136.81) * mm, "radius": 6.35 * mm});
            skCircle(sketch, "E18.2.4.0", {"center": v(-875.08, -174.91) * mm, "radius": 6.35 * mm});
            skCircle(sketch, "E18.2.5.0", {"center": v(-875.08, -213.01) * mm, "radius": 6.35 * mm});
            skCircle(sketch, "E18.2.6.0", {"center": v(-875.08, -251.11) * mm, "radius": 6.35 * mm});
            skCircle(sketch, "E18.2.7.0", {"center": v(-875.08, -289.21) * mm, "radius": 6.35 * mm});
            skCircle(sketch, "E18.3.0.0", {"center": v(-836.98, -22.51) * mm, "radius": 6.35 * mm});
            skCircle(sketch, "E18.3.1.0", {"center": v(-836.98, -60.61) * mm, "radius": 6.35 * mm});
            skCircle(sketch, "E18.3.2.0", {"center": v(-836.98, -98.71) * mm, "radius": 6.35 * mm});
            skCircle(sketch, "E18.3.3.0", {"center": v(-836.98, -136.81) * mm, "radius": 6.35 * mm});
            skCircle(sketch, "E18.3.4.0", {"center": v(-836.98, -174.91) * mm, "radius": 6.35 * mm});
            skCircle(sketch, "E18.3.5.0", {"center": v(-836.98, -213.01) * mm, "radius": 6.35 * mm});
            skCircle(sketch, "E18.3.6.0", {"center": v(-836.98, -251.11) * mm, "radius": 6.35 * mm});
            skCircle(sketch, "E18.3.7.0", {"center": v(-836.98, -289.21) * mm, "radius": 6.35 * mm});
            skCircle(sketch, "E18.4.0.0", {"center": v(-798.88, -22.51) * mm, "radius": 6.35 * mm});
            skCircle(sketch, "E18.4.1.0", {"center": v(-798.88, -60.61) * mm, "radius": 6.35 * mm});
            skCircle(sketch, "E18.4.2.0", {"center": v(-798.88, -98.71) * mm, "radius": 6.35 * mm});
            skCircle(sketch, "E18.4.3.0", {"center": v(-798.88, -136.81) * mm, "radius": 6.35 * mm});
            skCircle(sketch, "E18.4.4.0", {"center": v(-798.88, -174.91) * mm, "radius": 6.35 * mm});
            skCircle(sketch, "E18.4.5.0", {"center": v(-798.88, -213.01) * mm, "radius": 6.35 * mm});
            skCircle(sketch, "E18.4.6.0", {"center": v(-798.88, -251.11) * mm, "radius": 6.35 * mm});
            skCircle(sketch, "E18.4.7.0", {"center": v(-798.88, -289.21) * mm, "radius": 6.35 * mm});
            skCircle(sketch, "E18.5.0.0", {"center": v(-760.78, -22.51) * mm, "radius": 6.35 * mm});
            skCircle(sketch, "E18.5.1.0", {"center": v(-760.78, -60.61) * mm, "radius": 6.35 * mm});
            skCircle(sketch, "E18.5.2.0", {"center": v(-760.78, -98.71) * mm, "radius": 6.35 * mm});
            skCircle(sketch, "E18.5.3.0", {"center": v(-760.78, -136.81) * mm, "radius": 6.35 * mm});
            skCircle(sketch, "E18.5.4.0", {"center": v(-760.78, -174.91) * mm, "radius": 6.35 * mm});
            skCircle(sketch, "E18.5.5.0", {"center": v(-760.78, -213.01) * mm, "radius": 6.35 * mm});
            skCircle(sketch, "E18.5.6.0", {"center": v(-760.78, -251.11) * mm, "radius": 6.35 * mm});
            skCircle(sketch, "E18.5.7.0", {"center": v(-760.78, -289.21) * mm, "radius": 6.35 * mm});
            skCircle(sketch, "E18.6.0.0", {"center": v(-722.68, -22.51) * mm, "radius": 6.35 * mm});
            skCircle(sketch, "E18.6.1.0", {"center": v(-722.68, -60.61) * mm, "radius": 6.35 * mm});
            skCircle(sketch, "E18.6.2.0", {"center": v(-722.68, -98.71) * mm, "radius": 6.35 * mm});
            skCircle(sketch, "E18.6.3.0", {"center": v(-722.68, -136.81) * mm, "radius": 6.35 * mm});
            skCircle(sketch, "E18.6.4.0", {"center": v(-722.68, -174.91) * mm, "radius": 6.35 * mm});
            skCircle(sketch, "E18.6.5.0", {"center": v(-722.68, -213.01) * mm, "radius": 6.35 * mm});
            skCircle(sketch, "E18.6.6.0", {"center": v(-722.68, -251.11) * mm, "radius": 6.35 * mm});
            skCircle(sketch, "E18.6.7.0", {"center": v(-722.68, -289.21) * mm, "radius": 6.35 * mm});
            skCircle(sketch, "E18.7.0.0", {"center": v(-684.58, -22.51) * mm, "radius": 6.35 * mm});
            skCircle(sketch, "E18.7.1.0", {"center": v(-684.58, -60.61) * mm, "radius": 6.35 * mm});
            skCircle(sketch, "E18.7.2.0", {"center": v(-684.58, -98.71) * mm, "radius": 6.35 * mm});
            skCircle(sketch, "E18.7.3.0", {"center": v(-684.58, -136.81) * mm, "radius": 6.35 * mm});
            skCircle(sketch, "E18.7.4.0", {"center": v(-684.58, -174.91) * mm, "radius": 6.35 * mm});
            skCircle(sketch, "E18.7.5.0", {"center": v(-684.58, -213.01) * mm, "radius": 6.35 * mm});
            skCircle(sketch, "E18.7.6.0", {"center": v(-684.58, -251.11) * mm, "radius": 6.35 * mm});
            skCircle(sketch, "E18.7.7.0", {"center": v(-684.58, -289.21) * mm, "radius": 6.35 * mm});
            skLineSegment(sketch, "E18.direction1", {"start": v(-951.28, -22.51) * mm, "end": v(-913.18, -22.51) * mm, "construction": true});
            skLineSegment(sketch, "E18.direction2", {"start": v(-951.28, -22.51) * mm, "end": v(-951.28, -60.61) * mm, "construction": true});
            skSolve(sketch);
        }
        {
            var Q0;
            Q0 = qSketchRegion(id + "F6", true);
            extrude(context, id + "F7", {"entities" : qUnion([Q0]), "operationType" : NewBodyOperationType.REMOVE, "endBound" : BoundingType.THROUGH_ALL, "oppositeDirection" : true, "depth" : 25.4 * mm});
        }
        {
            var Q0;
            Q0=makeQuery(id+"F1.opExtrude","CAP_FACE",FACE,{"disambiguationData":[OSD([sQuery(id+"F0.wireOp",EDGE,"E0.rect.bottom"),sQuery(id+"F0.wireOp",EDGE,"E0.rect.top"),sQuery(id+"F0.wireOp",EDGE,"E0.rect.left"),sQuery(id+"F0.wireOp",EDGE,"E0.rect.right"),sQuery(id+"F0.wireOp",EDGE,"E1.0"),sQuery(id+"F0.wireOp",EDGE,"E2.0"),sQuery(id+"F0.wireOp",EDGE,"E3.0"),sQuery(id+"F0.wireOp",EDGE,"E4.0"),sQuery(id+"F0.wireOp",EDGE,"E5.trimOffspring"),sQuery(id+"F0.wireOp",EDGE,"E6.trimOffspring"),sQuery(id+"F0.wireOp",EDGE,"E7.trimOffspring"),sQuery(id+"F0.wireOp",EDGE,"E8.trimOffspring")])],"isStart":false});
            var sketch = newSketch(context, id + "F8", { "sketchPlane" : qUnion([Q0])});
            skCircle(sketch, "E19.0", {"center": v(-634.04, 111.8) * mm, "radius": 6.35 * mm});
            skCircle(sketch, "E20.0.1.0", {"center": v(-634.04, 73.7) * mm, "radius": 6.35 * mm});
            skCircle(sketch, "E20.0.2.0", {"center": v(-634.04, 35.6) * mm, "radius": 6.35 * mm});
            skCircle(sketch, "E20.0.3.0", {"center": v(-634.04, -2.5) * mm, "radius": 6.35 * mm});
            skCircle(sketch, "E20.0.4.0", {"center": v(-634.04, -40.6) * mm, "radius": 6.35 * mm});
            skCircle(sketch, "E20.0.5.0", {"center": v(-634.04, -78.7) * mm, "radius": 6.35 * mm});
            skCircle(sketch, "E20.0.6.0", {"center": v(-634.04, -116.8) * mm, "radius": 6.35 * mm});
            skCircle(sketch, "E20.0.7.0", {"center": v(-634.04, -154.9) * mm, "radius": 6.35 * mm});
            skCircle(sketch, "E20.0.8.0", {"center": v(-634.04, -193) * mm, "radius": 6.35 * mm});
            skCircle(sketch, "E20.0.9.0", {"center": v(-634.04, -231.1) * mm, "radius": 6.35 * mm});
            skCircle(sketch, "E20.0.10.0", {"center": v(-634.04, -269.2) * mm, "radius": 6.35 * mm});
            skCircle(sketch, "E20.0.11.0", {"center": v(-634.04, -307.3) * mm, "radius": 6.35 * mm});
            skCircle(sketch, "E20.0.12.0", {"center": v(-634.04, -345.4) * mm, "radius": 6.35 * mm});
            skCircle(sketch, "E20.0.13.0", {"center": v(-634.04, -383.5) * mm, "radius": 6.35 * mm});
            skCircle(sketch, "E20.0.14.0", {"center": v(-634.04, -421.6) * mm, "radius": 6.35 * mm});
            skCircle(sketch, "E20.0.15.0", {"center": v(-634.04, -459.7) * mm, "radius": 6.35 * mm});
            skCircle(sketch, "E20.0.16.0", {"center": v(-634.04, -497.8) * mm, "radius": 6.35 * mm});
            skCircle(sketch, "E20.0.17.0", {"center": v(-634.04, -535.9) * mm, "radius": 6.35 * mm});
            skCircle(sketch, "E20.0.18.0", {"center": v(-634.04, -574) * mm, "radius": 6.35 * mm});
            skCircle(sketch, "E20.0.19.0", {"center": v(-634.04, -612.1) * mm, "radius": 6.35 * mm});
            skCircle(sketch, "E20.1.0.0", {"center": v(-595.94, 111.8) * mm, "radius": 6.35 * mm});
            skCircle(sketch, "E20.1.1.0", {"center": v(-595.94, 73.7) * mm, "radius": 6.35 * mm});
            skCircle(sketch, "E20.1.2.0", {"center": v(-595.94, 35.6) * mm, "radius": 6.35 * mm});
            skCircle(sketch, "E20.1.3.0", {"center": v(-595.94, -2.5) * mm, "radius": 6.35 * mm});
            skCircle(sketch, "E20.1.4.0", {"center": v(-595.94, -40.6) * mm, "radius": 6.35 * mm});
            skCircle(sketch, "E20.1.5.0", {"center": v(-595.94, -78.7) * mm, "radius": 6.35 * mm});
            skCircle(sketch, "E20.1.6.0", {"center": v(-595.94, -116.8) * mm, "radius": 6.35 * mm});
            skCircle(sketch, "E20.1.7.0", {"center": v(-595.94, -154.9) * mm, "radius": 6.35 * mm});
            skCircle(sketch, "E20.1.8.0", {"center": v(-595.94, -193) * mm, "radius": 6.35 * mm});
            skCircle(sketch, "E20.1.9.0", {"center": v(-595.94, -231.1) * mm, "radius": 6.35 * mm});
            skCircle(sketch, "E20.1.10.0", {"center": v(-595.94, -269.2) * mm, "radius": 6.35 * mm});
            skCircle(sketch, "E20.1.11.0", {"center": v(-595.94, -307.3) * mm, "radius": 6.35 * mm});
            skCircle(sketch, "E20.1.12.0", {"center": v(-595.94, -345.4) * mm, "radius": 6.35 * mm});
            skCircle(sketch, "E20.1.13.0", {"center": v(-595.94, -383.5) * mm, "radius": 6.35 * mm});
            skCircle(sketch, "E20.1.14.0", {"center": v(-595.94, -421.6) * mm, "radius": 6.35 * mm});
            skCircle(sketch, "E20.1.15.0", {"center": v(-595.94, -459.7) * mm, "radius": 6.35 * mm});
            skCircle(sketch, "E20.1.16.0", {"center": v(-595.94, -497.8) * mm, "radius": 6.35 * mm});
            skCircle(sketch, "E20.1.17.0", {"center": v(-595.94, -535.9) * mm, "radius": 6.35 * mm});
            skCircle(sketch, "E20.1.18.0", {"center": v(-595.94, -574) * mm, "radius": 6.35 * mm});
            skCircle(sketch, "E20.1.19.0", {"center": v(-595.94, -612.1) * mm, "radius": 6.35 * mm});
            skCircle(sketch, "E20.2.0.0", {"center": v(-557.84, 111.8) * mm, "radius": 6.35 * mm});
            skCircle(sketch, "E20.2.1.0", {"center": v(-557.84, 73.7) * mm, "radius": 6.35 * mm});
            skCircle(sketch, "E20.2.2.0", {"center": v(-557.84, 35.6) * mm, "radius": 6.35 * mm});
            skCircle(sketch, "E20.2.3.0", {"center": v(-557.84, -2.5) * mm, "radius": 6.35 * mm});
            skCircle(sketch, "E20.2.4.0", {"center": v(-557.84, -40.6) * mm, "radius": 6.35 * mm});
            skCircle(sketch, "E20.2.5.0", {"center": v(-557.84, -78.7) * mm, "radius": 6.35 * mm});
            skCircle(sketch, "E20.2.6.0", {"center": v(-557.84, -116.8) * mm, "radius": 6.35 * mm});
            skCircle(sketch, "E20.2.7.0", {"center": v(-557.84, -154.9) * mm, "radius": 6.35 * mm});
            skCircle(sketch, "E20.2.8.0", {"center": v(-557.84, -193) * mm, "radius": 6.35 * mm});
            skCircle(sketch, "E20.2.9.0", {"center": v(-557.84, -231.1) * mm, "radius": 6.35 * mm});
            skCircle(sketch, "E20.2.10.0", {"center": v(-557.84, -269.2) * mm, "radius": 6.35 * mm});
            skCircle(sketch, "E20.2.11.0", {"center": v(-557.84, -307.3) * mm, "radius": 6.35 * mm});
            skCircle(sketch, "E20.2.12.0", {"center": v(-557.84, -345.4) * mm, "radius": 6.35 * mm});
            skCircle(sketch, "E20.2.13.0", {"center": v(-557.84, -383.5) * mm, "radius": 6.35 * mm});
            skCircle(sketch, "E20.2.14.0", {"center": v(-557.84, -421.6) * mm, "radius": 6.35 * mm});
            skCircle(sketch, "E20.2.15.0", {"center": v(-557.84, -459.7) * mm, "radius": 6.35 * mm});
            skCircle(sketch, "E20.2.16.0", {"center": v(-557.84, -497.8) * mm, "radius": 6.35 * mm});
            skCircle(sketch, "E20.2.17.0", {"center": v(-557.84, -535.9) * mm, "radius": 6.35 * mm});
            skCircle(sketch, "E20.2.18.0", {"center": v(-557.84, -574) * mm, "radius": 6.35 * mm});
            skCircle(sketch, "E20.2.19.0", {"center": v(-557.84, -612.1) * mm, "radius": 6.35 * mm});
            skCircle(sketch, "E20.3.0.0", {"center": v(-519.74, 111.8) * mm, "radius": 6.35 * mm});
            skCircle(sketch, "E20.3.1.0", {"center": v(-519.74, 73.7) * mm, "radius": 6.35 * mm});
            skCircle(sketch, "E20.3.2.0", {"center": v(-519.74, 35.6) * mm, "radius": 6.35 * mm});
            skCircle(sketch, "E20.3.3.0", {"center": v(-519.74, -2.5) * mm, "radius": 6.35 * mm});
            skCircle(sketch, "E20.3.4.0", {"center": v(-519.74, -40.6) * mm, "radius": 6.35 * mm});
            skCircle(sketch, "E20.3.5.0", {"center": v(-519.74, -78.7) * mm, "radius": 6.35 * mm});
            skCircle(sketch, "E20.3.6.0", {"center": v(-519.74, -116.8) * mm, "radius": 6.35 * mm});
            skCircle(sketch, "E20.3.7.0", {"center": v(-519.74, -154.9) * mm, "radius": 6.35 * mm});
            skCircle(sketch, "E20.3.8.0", {"center": v(-519.74, -193) * mm, "radius": 6.35 * mm});
            skCircle(sketch, "E20.3.9.0", {"center": v(-519.74, -231.1) * mm, "radius": 6.35 * mm});
            skCircle(sketch, "E20.3.10.0", {"center": v(-519.74, -269.2) * mm, "radius": 6.35 * mm});
            skCircle(sketch, "E20.3.11.0", {"center": v(-519.74, -307.3) * mm, "radius": 6.35 * mm});
            skCircle(sketch, "E20.3.12.0", {"center": v(-519.74, -345.4) * mm, "radius": 6.35 * mm});
            skCircle(sketch, "E20.3.13.0", {"center": v(-519.74, -383.5) * mm, "radius": 6.35 * mm});
            skCircle(sketch, "E20.3.14.0", {"center": v(-519.74, -421.6) * mm, "radius": 6.35 * mm});
            skCircle(sketch, "E20.3.15.0", {"center": v(-519.74, -459.7) * mm, "radius": 6.35 * mm});
            skCircle(sketch, "E20.3.16.0", {"center": v(-519.74, -497.8) * mm, "radius": 6.35 * mm});
            skCircle(sketch, "E20.3.17.0", {"center": v(-519.74, -535.9) * mm, "radius": 6.35 * mm});
            skCircle(sketch, "E20.3.18.0", {"center": v(-519.74, -574) * mm, "radius": 6.35 * mm});
            skCircle(sketch, "E20.3.19.0", {"center": v(-519.74, -612.1) * mm, "radius": 6.35 * mm});
            skCircle(sketch, "E20.4.0.0", {"center": v(-481.64, 111.8) * mm, "radius": 6.35 * mm});
            skCircle(sketch, "E20.4.1.0", {"center": v(-481.64, 73.7) * mm, "radius": 6.35 * mm});
            skCircle(sketch, "E20.4.2.0", {"center": v(-481.64, 35.6) * mm, "radius": 6.35 * mm});
            skCircle(sketch, "E20.4.3.0", {"center": v(-481.64, -2.5) * mm, "radius": 6.35 * mm});
            skCircle(sketch, "E20.4.4.0", {"center": v(-481.64, -40.6) * mm, "radius": 6.35 * mm});
            skCircle(sketch, "E20.4.5.0", {"center": v(-481.64, -78.7) * mm, "radius": 6.35 * mm});
            skCircle(sketch, "E20.4.6.0", {"center": v(-481.64, -116.8) * mm, "radius": 6.35 * mm});
            skCircle(sketch, "E20.4.7.0", {"center": v(-481.64, -154.9) * mm, "radius": 6.35 * mm});
            skCircle(sketch, "E20.4.8.0", {"center": v(-481.64, -193) * mm, "radius": 6.35 * mm});
            skCircle(sketch, "E20.4.9.0", {"center": v(-481.64, -231.1) * mm, "radius": 6.35 * mm});
            skCircle(sketch, "E20.4.10.0", {"center": v(-481.64, -269.2) * mm, "radius": 6.35 * mm});
            skCircle(sketch, "E20.4.11.0", {"center": v(-481.64, -307.3) * mm, "radius": 6.35 * mm});
            skCircle(sketch, "E20.4.12.0", {"center": v(-481.64, -345.4) * mm, "radius": 6.35 * mm});
            skCircle(sketch, "E20.4.13.0", {"center": v(-481.64, -383.5) * mm, "radius": 6.35 * mm});
            skCircle(sketch, "E20.4.14.0", {"center": v(-481.64, -421.6) * mm, "radius": 6.35 * mm});
            skCircle(sketch, "E20.4.15.0", {"center": v(-481.64, -459.7) * mm, "radius": 6.35 * mm});
            skCircle(sketch, "E20.4.16.0", {"center": v(-481.64, -497.8) * mm, "radius": 6.35 * mm});
            skCircle(sketch, "E20.4.17.0", {"center": v(-481.64, -535.9) * mm, "radius": 6.35 * mm});
            skCircle(sketch, "E20.4.18.0", {"center": v(-481.64, -574) * mm, "radius": 6.35 * mm});
            skCircle(sketch, "E20.4.19.0", {"center": v(-481.64, -612.1) * mm, "radius": 6.35 * mm});
            skCircle(sketch, "E20.5.0.0", {"center": v(-443.54, 111.8) * mm, "radius": 6.35 * mm});
            skCircle(sketch, "E20.5.1.0", {"center": v(-443.54, 73.7) * mm, "radius": 6.35 * mm});
            skCircle(sketch, "E20.5.2.0", {"center": v(-443.54, 35.6) * mm, "radius": 6.35 * mm});
            skCircle(sketch, "E20.5.3.0", {"center": v(-443.54, -2.5) * mm, "radius": 6.35 * mm});
            skCircle(sketch, "E20.5.4.0", {"center": v(-443.54, -40.6) * mm, "radius": 6.35 * mm});
            skCircle(sketch, "E20.5.5.0", {"center": v(-443.54, -78.7) * mm, "radius": 6.35 * mm});
            skCircle(sketch, "E20.5.6.0", {"center": v(-443.54, -116.8) * mm, "radius": 6.35 * mm});
            skCircle(sketch, "E20.5.7.0", {"center": v(-443.54, -154.9) * mm, "radius": 6.35 * mm});
            skCircle(sketch, "E20.5.8.0", {"center": v(-443.54, -193) * mm, "radius": 6.35 * mm});
            skCircle(sketch, "E20.5.9.0", {"center": v(-443.54, -231.1) * mm, "radius": 6.35 * mm});
            skCircle(sketch, "E20.5.10.0", {"center": v(-443.54, -269.2) * mm, "radius": 6.35 * mm});
            skCircle(sketch, "E20.5.11.0", {"center": v(-443.54, -307.3) * mm, "radius": 6.35 * mm});
            skCircle(sketch, "E20.5.12.0", {"center": v(-443.54, -345.4) * mm, "radius": 6.35 * mm});
            skCircle(sketch, "E20.5.13.0", {"center": v(-443.54, -383.5) * mm, "radius": 6.35 * mm});
            skCircle(sketch, "E20.5.14.0", {"center": v(-443.54, -421.6) * mm, "radius": 6.35 * mm});
            skCircle(sketch, "E20.5.15.0", {"center": v(-443.54, -459.7) * mm, "radius": 6.35 * mm});
            skCircle(sketch, "E20.5.16.0", {"center": v(-443.54, -497.8) * mm, "radius": 6.35 * mm});
            skCircle(sketch, "E20.5.17.0", {"center": v(-443.54, -535.9) * mm, "radius": 6.35 * mm});
            skCircle(sketch, "E20.5.18.0", {"center": v(-443.54, -574) * mm, "radius": 6.35 * mm});
            skCircle(sketch, "E20.5.19.0", {"center": v(-443.54, -612.1) * mm, "radius": 6.35 * mm});
            skCircle(sketch, "E20.6.0.0", {"center": v(-405.44, 111.8) * mm, "radius": 6.35 * mm});
            skCircle(sketch, "E20.6.1.0", {"center": v(-405.44, 73.7) * mm, "radius": 6.35 * mm});
            skCircle(sketch, "E20.6.2.0", {"center": v(-405.44, 35.6) * mm, "radius": 6.35 * mm});
            skCircle(sketch, "E20.6.3.0", {"center": v(-405.44, -2.5) * mm, "radius": 6.35 * mm});
            skCircle(sketch, "E20.6.4.0", {"center": v(-405.44, -40.6) * mm, "radius": 6.35 * mm});
            skCircle(sketch, "E20.6.5.0", {"center": v(-405.44, -78.7) * mm, "radius": 6.35 * mm});
            skCircle(sketch, "E20.6.6.0", {"center": v(-405.44, -116.8) * mm, "radius": 6.35 * mm});
            skCircle(sketch, "E20.6.7.0", {"center": v(-405.44, -154.9) * mm, "radius": 6.35 * mm});
            skCircle(sketch, "E20.6.8.0", {"center": v(-405.44, -193) * mm, "radius": 6.35 * mm});
            skCircle(sketch, "E20.6.9.0", {"center": v(-405.44, -231.1) * mm, "radius": 6.35 * mm});
            skCircle(sketch, "E20.6.10.0", {"center": v(-405.44, -269.2) * mm, "radius": 6.35 * mm});
            skCircle(sketch, "E20.6.11.0", {"center": v(-405.44, -307.3) * mm, "radius": 6.35 * mm});
            skCircle(sketch, "E20.6.12.0", {"center": v(-405.44, -345.4) * mm, "radius": 6.35 * mm});
            skCircle(sketch, "E20.6.13.0", {"center": v(-405.44, -383.5) * mm, "radius": 6.35 * mm});
            skCircle(sketch, "E20.6.14.0", {"center": v(-405.44, -421.6) * mm, "radius": 6.35 * mm});
            skCircle(sketch, "E20.6.15.0", {"center": v(-405.44, -459.7) * mm, "radius": 6.35 * mm});
            skCircle(sketch, "E20.6.16.0", {"center": v(-405.44, -497.8) * mm, "radius": 6.35 * mm});
            skCircle(sketch, "E20.6.17.0", {"center": v(-405.44, -535.9) * mm, "radius": 6.35 * mm});
            skCircle(sketch, "E20.6.18.0", {"center": v(-405.44, -574) * mm, "radius": 6.35 * mm});
            skCircle(sketch, "E20.6.19.0", {"center": v(-405.44, -612.1) * mm, "radius": 6.35 * mm});
            skCircle(sketch, "E20.7.0.0", {"center": v(-367.34, 111.8) * mm, "radius": 6.35 * mm});
            skCircle(sketch, "E20.7.1.0", {"center": v(-367.34, 73.7) * mm, "radius": 6.35 * mm});
            skCircle(sketch, "E20.7.2.0", {"center": v(-367.34, 35.6) * mm, "radius": 6.35 * mm});
            skCircle(sketch, "E20.7.3.0", {"center": v(-367.34, -2.5) * mm, "radius": 6.35 * mm});
            skCircle(sketch, "E20.7.4.0", {"center": v(-367.34, -40.6) * mm, "radius": 6.35 * mm});
            skCircle(sketch, "E20.7.5.0", {"center": v(-367.34, -78.7) * mm, "radius": 6.35 * mm});
            skCircle(sketch, "E20.7.6.0", {"center": v(-367.34, -116.8) * mm, "radius": 6.35 * mm});
            skCircle(sketch, "E20.7.7.0", {"center": v(-367.34, -154.9) * mm, "radius": 6.35 * mm});
            skCircle(sketch, "E20.7.8.0", {"center": v(-367.34, -193) * mm, "radius": 6.35 * mm});
            skCircle(sketch, "E20.7.9.0", {"center": v(-367.34, -231.1) * mm, "radius": 6.35 * mm});
            skCircle(sketch, "E20.7.10.0", {"center": v(-367.34, -269.2) * mm, "radius": 6.35 * mm});
            skCircle(sketch, "E20.7.11.0", {"center": v(-367.34, -307.3) * mm, "radius": 6.35 * mm});
            skCircle(sketch, "E20.7.12.0", {"center": v(-367.34, -345.4) * mm, "radius": 6.35 * mm});
            skCircle(sketch, "E20.7.13.0", {"center": v(-367.34, -383.5) * mm, "radius": 6.35 * mm});
            skCircle(sketch, "E20.7.14.0", {"center": v(-367.34, -421.6) * mm, "radius": 6.35 * mm});
            skCircle(sketch, "E20.7.15.0", {"center": v(-367.34, -459.7) * mm, "radius": 6.35 * mm});
            skCircle(sketch, "E20.7.16.0", {"center": v(-367.34, -497.8) * mm, "radius": 6.35 * mm});
            skCircle(sketch, "E20.7.17.0", {"center": v(-367.34, -535.9) * mm, "radius": 6.35 * mm});
            skCircle(sketch, "E20.7.18.0", {"center": v(-367.34, -574) * mm, "radius": 6.35 * mm});
            skCircle(sketch, "E20.7.19.0", {"center": v(-367.34, -612.1) * mm, "radius": 6.35 * mm});
            skCircle(sketch, "E20.8.0.0", {"center": v(-329.24, 111.8) * mm, "radius": 6.35 * mm});
            skCircle(sketch, "E20.8.1.0", {"center": v(-329.24, 73.7) * mm, "radius": 6.35 * mm});
            skCircle(sketch, "E20.8.2.0", {"center": v(-329.24, 35.6) * mm, "radius": 6.35 * mm});
            skCircle(sketch, "E20.8.3.0", {"center": v(-329.24, -2.5) * mm, "radius": 6.35 * mm});
            skCircle(sketch, "E20.8.4.0", {"center": v(-329.24, -40.6) * mm, "radius": 6.35 * mm});
            skCircle(sketch, "E20.8.5.0", {"center": v(-329.24, -78.7) * mm, "radius": 6.35 * mm});
            skCircle(sketch, "E20.8.6.0", {"center": v(-329.24, -116.8) * mm, "radius": 6.35 * mm});
            skCircle(sketch, "E20.8.7.0", {"center": v(-329.24, -154.9) * mm, "radius": 6.35 * mm});
            skCircle(sketch, "E20.8.8.0", {"center": v(-329.24, -193) * mm, "radius": 6.35 * mm});
            skCircle(sketch, "E20.8.9.0", {"center": v(-329.24, -231.1) * mm, "radius": 6.35 * mm});
            skCircle(sketch, "E20.8.10.0", {"center": v(-329.24, -269.2) * mm, "radius": 6.35 * mm});
            skCircle(sketch, "E20.8.11.0", {"center": v(-329.24, -307.3) * mm, "radius": 6.35 * mm});
            skCircle(sketch, "E20.8.12.0", {"center": v(-329.24, -345.4) * mm, "radius": 6.35 * mm});
            skCircle(sketch, "E20.8.13.0", {"center": v(-329.24, -383.5) * mm, "radius": 6.35 * mm});
            skCircle(sketch, "E20.8.14.0", {"center": v(-329.24, -421.6) * mm, "radius": 6.35 * mm});
            skCircle(sketch, "E20.8.15.0", {"center": v(-329.24, -459.7) * mm, "radius": 6.35 * mm});
            skCircle(sketch, "E20.8.16.0", {"center": v(-329.24, -497.8) * mm, "radius": 6.35 * mm});
            skCircle(sketch, "E20.8.17.0", {"center": v(-329.24, -535.9) * mm, "radius": 6.35 * mm});
            skCircle(sketch, "E20.8.18.0", {"center": v(-329.24, -574) * mm, "radius": 6.35 * mm});
            skCircle(sketch, "E20.8.19.0", {"center": v(-329.24, -612.1) * mm, "radius": 6.35 * mm});
            skCircle(sketch, "E20.9.0.0", {"center": v(-291.14, 111.8) * mm, "radius": 6.35 * mm});
            skCircle(sketch, "E20.9.1.0", {"center": v(-291.14, 73.7) * mm, "radius": 6.35 * mm});
            skCircle(sketch, "E20.9.2.0", {"center": v(-291.14, 35.6) * mm, "radius": 6.35 * mm});
            skCircle(sketch, "E20.9.3.0", {"center": v(-291.14, -2.5) * mm, "radius": 6.35 * mm});
            skCircle(sketch, "E20.9.4.0", {"center": v(-291.14, -40.6) * mm, "radius": 6.35 * mm});
            skCircle(sketch, "E20.9.5.0", {"center": v(-291.14, -78.7) * mm, "radius": 6.35 * mm});
            skCircle(sketch, "E20.9.6.0", {"center": v(-291.14, -116.8) * mm, "radius": 6.35 * mm});
            skCircle(sketch, "E20.9.7.0", {"center": v(-291.14, -154.9) * mm, "radius": 6.35 * mm});
            skCircle(sketch, "E20.9.8.0", {"center": v(-291.14, -193) * mm, "radius": 6.35 * mm});
            skCircle(sketch, "E20.9.9.0", {"center": v(-291.14, -231.1) * mm, "radius": 6.35 * mm});
            skCircle(sketch, "E20.9.10.0", {"center": v(-291.14, -269.2) * mm, "radius": 6.35 * mm});
            skCircle(sketch, "E20.9.11.0", {"center": v(-291.14, -307.3) * mm, "radius": 6.35 * mm});
            skCircle(sketch, "E20.9.12.0", {"center": v(-291.14, -345.4) * mm, "radius": 6.35 * mm});
            skCircle(sketch, "E20.9.13.0", {"center": v(-291.14, -383.5) * mm, "radius": 6.35 * mm});
            skCircle(sketch, "E20.9.14.0", {"center": v(-291.14, -421.6) * mm, "radius": 6.35 * mm});
            skCircle(sketch, "E20.9.15.0", {"center": v(-291.14, -459.7) * mm, "radius": 6.35 * mm});
            skCircle(sketch, "E20.9.16.0", {"center": v(-291.14, -497.8) * mm, "radius": 6.35 * mm});
            skCircle(sketch, "E20.9.17.0", {"center": v(-291.14, -535.9) * mm, "radius": 6.35 * mm});
            skCircle(sketch, "E20.9.18.0", {"center": v(-291.14, -574) * mm, "radius": 6.35 * mm});
            skCircle(sketch, "E20.9.19.0", {"center": v(-291.14, -612.1) * mm, "radius": 6.35 * mm});
            skCircle(sketch, "E20.10.0.0", {"center": v(-253.04, 111.8) * mm, "radius": 6.35 * mm});
            skCircle(sketch, "E20.10.1.0", {"center": v(-253.04, 73.7) * mm, "radius": 6.35 * mm});
            skCircle(sketch, "E20.10.2.0", {"center": v(-253.04, 35.6) * mm, "radius": 6.35 * mm});
            skCircle(sketch, "E20.10.3.0", {"center": v(-253.04, -2.5) * mm, "radius": 6.35 * mm});
            skCircle(sketch, "E20.10.4.0", {"center": v(-253.04, -40.6) * mm, "radius": 6.35 * mm});
            skCircle(sketch, "E20.10.5.0", {"center": v(-253.04, -78.7) * mm, "radius": 6.35 * mm});
            skCircle(sketch, "E20.10.6.0", {"center": v(-253.04, -116.8) * mm, "radius": 6.35 * mm});
            skCircle(sketch, "E20.10.7.0", {"center": v(-253.04, -154.9) * mm, "radius": 6.35 * mm});
            skCircle(sketch, "E20.10.8.0", {"center": v(-253.04, -193) * mm, "radius": 6.35 * mm});
            skCircle(sketch, "E20.10.9.0", {"center": v(-253.04, -231.1) * mm, "radius": 6.35 * mm});
            skCircle(sketch, "E20.10.10.0", {"center": v(-253.04, -269.2) * mm, "radius": 6.35 * mm});
            skCircle(sketch, "E20.10.11.0", {"center": v(-253.04, -307.3) * mm, "radius": 6.35 * mm});
            skCircle(sketch, "E20.10.12.0", {"center": v(-253.04, -345.4) * mm, "radius": 6.35 * mm});
            skCircle(sketch, "E20.10.13.0", {"center": v(-253.04, -383.5) * mm, "radius": 6.35 * mm});
            skCircle(sketch, "E20.10.14.0", {"center": v(-253.04, -421.6) * mm, "radius": 6.35 * mm});
            skCircle(sketch, "E20.10.15.0", {"center": v(-253.04, -459.7) * mm, "radius": 6.35 * mm});
            skCircle(sketch, "E20.10.16.0", {"center": v(-253.04, -497.8) * mm, "radius": 6.35 * mm});
            skCircle(sketch, "E20.10.17.0", {"center": v(-253.04, -535.9) * mm, "radius": 6.35 * mm});
            skCircle(sketch, "E20.10.18.0", {"center": v(-253.04, -574) * mm, "radius": 6.35 * mm});
            skCircle(sketch, "E20.10.19.0", {"center": v(-253.04, -612.1) * mm, "radius": 6.35 * mm});
            skCircle(sketch, "E20.11.0.0", {"center": v(-214.94, 111.8) * mm, "radius": 6.35 * mm});
            skCircle(sketch, "E20.11.1.0", {"center": v(-214.94, 73.7) * mm, "radius": 6.35 * mm});
            skCircle(sketch, "E20.11.2.0", {"center": v(-214.94, 35.6) * mm, "radius": 6.35 * mm});
            skCircle(sketch, "E20.11.3.0", {"center": v(-214.94, -2.5) * mm, "radius": 6.35 * mm});
            skCircle(sketch, "E20.11.4.0", {"center": v(-214.94, -40.6) * mm, "radius": 6.35 * mm});
            skCircle(sketch, "E20.11.5.0", {"center": v(-214.94, -78.7) * mm, "radius": 6.35 * mm});
            skCircle(sketch, "E20.11.6.0", {"center": v(-214.94, -116.8) * mm, "radius": 6.35 * mm});
            skCircle(sketch, "E20.11.7.0", {"center": v(-214.94, -154.9) * mm, "radius": 6.35 * mm});
            skCircle(sketch, "E20.11.8.0", {"center": v(-214.94, -193) * mm, "radius": 6.35 * mm});
            skCircle(sketch, "E20.11.9.0", {"center": v(-214.94, -231.1) * mm, "radius": 6.35 * mm});
            skCircle(sketch, "E20.11.10.0", {"center": v(-214.94, -269.2) * mm, "radius": 6.35 * mm});
            skCircle(sketch, "E20.11.11.0", {"center": v(-214.94, -307.3) * mm, "radius": 6.35 * mm});
            skCircle(sketch, "E20.11.12.0", {"center": v(-214.94, -345.4) * mm, "radius": 6.35 * mm});
            skCircle(sketch, "E20.11.13.0", {"center": v(-214.94, -383.5) * mm, "radius": 6.35 * mm});
            skCircle(sketch, "E20.11.14.0", {"center": v(-214.94, -421.6) * mm, "radius": 6.35 * mm});
            skCircle(sketch, "E20.11.15.0", {"center": v(-214.94, -459.7) * mm, "radius": 6.35 * mm});
            skCircle(sketch, "E20.11.16.0", {"center": v(-214.94, -497.8) * mm, "radius": 6.35 * mm});
            skCircle(sketch, "E20.11.17.0", {"center": v(-214.94, -535.9) * mm, "radius": 6.35 * mm});
            skCircle(sketch, "E20.11.18.0", {"center": v(-214.94, -574) * mm, "radius": 6.35 * mm});
            skCircle(sketch, "E20.11.19.0", {"center": v(-214.94, -612.1) * mm, "radius": 6.35 * mm});
            skCircle(sketch, "E20.12.0.0", {"center": v(-176.84, 111.8) * mm, "radius": 6.35 * mm});
            skCircle(sketch, "E20.12.1.0", {"center": v(-176.84, 73.7) * mm, "radius": 6.35 * mm});
            skCircle(sketch, "E20.12.2.0", {"center": v(-176.84, 35.6) * mm, "radius": 6.35 * mm});
            skCircle(sketch, "E20.12.3.0", {"center": v(-176.84, -2.5) * mm, "radius": 6.35 * mm});
            skCircle(sketch, "E20.12.4.0", {"center": v(-176.84, -40.6) * mm, "radius": 6.35 * mm});
            skCircle(sketch, "E20.12.5.0", {"center": v(-176.84, -78.7) * mm, "radius": 6.35 * mm});
            skCircle(sketch, "E20.12.6.0", {"center": v(-176.84, -116.8) * mm, "radius": 6.35 * mm});
            skCircle(sketch, "E20.12.7.0", {"center": v(-176.84, -154.9) * mm, "radius": 6.35 * mm});
            skCircle(sketch, "E20.12.8.0", {"center": v(-176.84, -193) * mm, "radius": 6.35 * mm});
            skCircle(sketch, "E20.12.9.0", {"center": v(-176.84, -231.1) * mm, "radius": 6.35 * mm});
            skCircle(sketch, "E20.12.10.0", {"center": v(-176.84, -269.2) * mm, "radius": 6.35 * mm});
            skCircle(sketch, "E20.12.11.0", {"center": v(-176.84, -307.3) * mm, "radius": 6.35 * mm});
            skCircle(sketch, "E20.12.12.0", {"center": v(-176.84, -345.4) * mm, "radius": 6.35 * mm});
            skCircle(sketch, "E20.12.13.0", {"center": v(-176.84, -383.5) * mm, "radius": 6.35 * mm});
            skCircle(sketch, "E20.12.14.0", {"center": v(-176.84, -421.6) * mm, "radius": 6.35 * mm});
            skCircle(sketch, "E20.12.15.0", {"center": v(-176.84, -459.7) * mm, "radius": 6.35 * mm});
            skCircle(sketch, "E20.12.16.0", {"center": v(-176.84, -497.8) * mm, "radius": 6.35 * mm});
            skCircle(sketch, "E20.12.17.0", {"center": v(-176.84, -535.9) * mm, "radius": 6.35 * mm});
            skCircle(sketch, "E20.12.18.0", {"center": v(-176.84, -574) * mm, "radius": 6.35 * mm});
            skCircle(sketch, "E20.12.19.0", {"center": v(-176.84, -612.1) * mm, "radius": 6.35 * mm});
            skCircle(sketch, "E20.13.0.0", {"center": v(-138.74, 111.8) * mm, "radius": 6.35 * mm});
            skCircle(sketch, "E20.13.1.0", {"center": v(-138.74, 73.7) * mm, "radius": 6.35 * mm});
            skCircle(sketch, "E20.13.2.0", {"center": v(-138.74, 35.6) * mm, "radius": 6.35 * mm});
            skCircle(sketch, "E20.13.3.0", {"center": v(-138.74, -2.5) * mm, "radius": 6.35 * mm});
            skCircle(sketch, "E20.13.4.0", {"center": v(-138.74, -40.6) * mm, "radius": 6.35 * mm});
            skCircle(sketch, "E20.13.5.0", {"center": v(-138.74, -78.7) * mm, "radius": 6.35 * mm});
            skCircle(sketch, "E20.13.6.0", {"center": v(-138.74, -116.8) * mm, "radius": 6.35 * mm});
            skCircle(sketch, "E20.13.7.0", {"center": v(-138.74, -154.9) * mm, "radius": 6.35 * mm});
            skCircle(sketch, "E20.13.8.0", {"center": v(-138.74, -193) * mm, "radius": 6.35 * mm});
            skCircle(sketch, "E20.13.9.0", {"center": v(-138.74, -231.1) * mm, "radius": 6.35 * mm});
            skCircle(sketch, "E20.13.10.0", {"center": v(-138.74, -269.2) * mm, "radius": 6.35 * mm});
            skCircle(sketch, "E20.13.11.0", {"center": v(-138.74, -307.3) * mm, "radius": 6.35 * mm});
            skCircle(sketch, "E20.13.12.0", {"center": v(-138.74, -345.4) * mm, "radius": 6.35 * mm});
            skCircle(sketch, "E20.13.13.0", {"center": v(-138.74, -383.5) * mm, "radius": 6.35 * mm});
            skCircle(sketch, "E20.13.14.0", {"center": v(-138.74, -421.6) * mm, "radius": 6.35 * mm});
            skCircle(sketch, "E20.13.15.0", {"center": v(-138.74, -459.7) * mm, "radius": 6.35 * mm});
            skCircle(sketch, "E20.13.16.0", {"center": v(-138.74, -497.8) * mm, "radius": 6.35 * mm});
            skCircle(sketch, "E20.13.17.0", {"center": v(-138.74, -535.9) * mm, "radius": 6.35 * mm});
            skCircle(sketch, "E20.13.18.0", {"center": v(-138.74, -574) * mm, "radius": 6.35 * mm});
            skCircle(sketch, "E20.13.19.0", {"center": v(-138.74, -612.1) * mm, "radius": 6.35 * mm});
            skCircle(sketch, "E20.14.0.0", {"center": v(-100.64, 111.8) * mm, "radius": 6.35 * mm});
            skCircle(sketch, "E20.14.1.0", {"center": v(-100.64, 73.7) * mm, "radius": 6.35 * mm});
            skCircle(sketch, "E20.14.2.0", {"center": v(-100.64, 35.6) * mm, "radius": 6.35 * mm});
            skCircle(sketch, "E20.14.3.0", {"center": v(-100.64, -2.5) * mm, "radius": 6.35 * mm});
            skCircle(sketch, "E20.14.4.0", {"center": v(-100.64, -40.6) * mm, "radius": 6.35 * mm});
            skCircle(sketch, "E20.14.5.0", {"center": v(-100.64, -78.7) * mm, "radius": 6.35 * mm});
            skCircle(sketch, "E20.14.6.0", {"center": v(-100.64, -116.8) * mm, "radius": 6.35 * mm});
            skCircle(sketch, "E20.14.7.0", {"center": v(-100.64, -154.9) * mm, "radius": 6.35 * mm});
            skCircle(sketch, "E20.14.8.0", {"center": v(-100.64, -193) * mm, "radius": 6.35 * mm});
            skCircle(sketch, "E20.14.9.0", {"center": v(-100.64, -231.1) * mm, "radius": 6.35 * mm});
            skCircle(sketch, "E20.14.10.0", {"center": v(-100.64, -269.2) * mm, "radius": 6.35 * mm});
            skCircle(sketch, "E20.14.11.0", {"center": v(-100.64, -307.3) * mm, "radius": 6.35 * mm});
            skCircle(sketch, "E20.14.12.0", {"center": v(-100.64, -345.4) * mm, "radius": 6.35 * mm});
            skCircle(sketch, "E20.14.13.0", {"center": v(-100.64, -383.5) * mm, "radius": 6.35 * mm});
            skCircle(sketch, "E20.14.14.0", {"center": v(-100.64, -421.6) * mm, "radius": 6.35 * mm});
            skCircle(sketch, "E20.14.15.0", {"center": v(-100.64, -459.7) * mm, "radius": 6.35 * mm});
            skCircle(sketch, "E20.14.16.0", {"center": v(-100.64, -497.8) * mm, "radius": 6.35 * mm});
            skCircle(sketch, "E20.14.17.0", {"center": v(-100.64, -535.9) * mm, "radius": 6.35 * mm});
            skCircle(sketch, "E20.14.18.0", {"center": v(-100.64, -574) * mm, "radius": 6.35 * mm});
            skCircle(sketch, "E20.14.19.0", {"center": v(-100.64, -612.1) * mm, "radius": 6.35 * mm});
            skCircle(sketch, "E20.15.0.0", {"center": v(-62.54, 111.8) * mm, "radius": 6.35 * mm});
            skCircle(sketch, "E20.15.1.0", {"center": v(-62.54, 73.7) * mm, "radius": 6.35 * mm});
            skCircle(sketch, "E20.15.2.0", {"center": v(-62.54, 35.6) * mm, "radius": 6.35 * mm});
            skCircle(sketch, "E20.15.3.0", {"center": v(-62.54, -2.5) * mm, "radius": 6.35 * mm});
            skCircle(sketch, "E20.15.4.0", {"center": v(-62.54, -40.6) * mm, "radius": 6.35 * mm});
            skCircle(sketch, "E20.15.5.0", {"center": v(-62.54, -78.7) * mm, "radius": 6.35 * mm});
            skCircle(sketch, "E20.15.6.0", {"center": v(-62.54, -116.8) * mm, "radius": 6.35 * mm});
            skCircle(sketch, "E20.15.7.0", {"center": v(-62.54, -154.9) * mm, "radius": 6.35 * mm});
            skCircle(sketch, "E20.15.8.0", {"center": v(-62.54, -193) * mm, "radius": 6.35 * mm});
            skCircle(sketch, "E20.15.9.0", {"center": v(-62.54, -231.1) * mm, "radius": 6.35 * mm});
            skCircle(sketch, "E20.15.10.0", {"center": v(-62.54, -269.2) * mm, "radius": 6.35 * mm});
            skCircle(sketch, "E20.15.11.0", {"center": v(-62.54, -307.3) * mm, "radius": 6.35 * mm});
            skCircle(sketch, "E20.15.12.0", {"center": v(-62.54, -345.4) * mm, "radius": 6.35 * mm});
            skCircle(sketch, "E20.15.13.0", {"center": v(-62.54, -383.5) * mm, "radius": 6.35 * mm});
            skCircle(sketch, "E20.15.14.0", {"center": v(-62.54, -421.6) * mm, "radius": 6.35 * mm});
            skCircle(sketch, "E20.15.15.0", {"center": v(-62.54, -459.7) * mm, "radius": 6.35 * mm});
            skCircle(sketch, "E20.15.16.0", {"center": v(-62.54, -497.8) * mm, "radius": 6.35 * mm});
            skCircle(sketch, "E20.15.17.0", {"center": v(-62.54, -535.9) * mm, "radius": 6.35 * mm});
            skCircle(sketch, "E20.15.18.0", {"center": v(-62.54, -574) * mm, "radius": 6.35 * mm});
            skCircle(sketch, "E20.15.19.0", {"center": v(-62.54, -612.1) * mm, "radius": 6.35 * mm});
            skCircle(sketch, "E20.16.0.0", {"center": v(-24.44, 111.8) * mm, "radius": 6.35 * mm});
            skCircle(sketch, "E20.16.1.0", {"center": v(-24.44, 73.7) * mm, "radius": 6.35 * mm});
            skCircle(sketch, "E20.16.2.0", {"center": v(-24.44, 35.6) * mm, "radius": 6.35 * mm});
            skCircle(sketch, "E20.16.3.0", {"center": v(-24.44, -2.5) * mm, "radius": 6.35 * mm});
            skCircle(sketch, "E20.16.4.0", {"center": v(-24.44, -40.6) * mm, "radius": 6.35 * mm});
            skCircle(sketch, "E20.16.5.0", {"center": v(-24.44, -78.7) * mm, "radius": 6.35 * mm});
            skCircle(sketch, "E20.16.6.0", {"center": v(-24.44, -116.8) * mm, "radius": 6.35 * mm});
            skCircle(sketch, "E20.16.7.0", {"center": v(-24.44, -154.9) * mm, "radius": 6.35 * mm});
            skCircle(sketch, "E20.16.8.0", {"center": v(-24.44, -193) * mm, "radius": 6.35 * mm});
            skCircle(sketch, "E20.16.9.0", {"center": v(-24.44, -231.1) * mm, "radius": 6.35 * mm});
            skCircle(sketch, "E20.16.10.0", {"center": v(-24.44, -269.2) * mm, "radius": 6.35 * mm});
            skCircle(sketch, "E20.16.11.0", {"center": v(-24.44, -307.3) * mm, "radius": 6.35 * mm});
            skCircle(sketch, "E20.16.12.0", {"center": v(-24.44, -345.4) * mm, "radius": 6.35 * mm});
            skCircle(sketch, "E20.16.13.0", {"center": v(-24.44, -383.5) * mm, "radius": 6.35 * mm});
            skCircle(sketch, "E20.16.14.0", {"center": v(-24.44, -421.6) * mm, "radius": 6.35 * mm});
            skCircle(sketch, "E20.16.15.0", {"center": v(-24.44, -459.7) * mm, "radius": 6.35 * mm});
            skCircle(sketch, "E20.16.16.0", {"center": v(-24.44, -497.8) * mm, "radius": 6.35 * mm});
            skCircle(sketch, "E20.16.17.0", {"center": v(-24.44, -535.9) * mm, "radius": 6.35 * mm});
            skCircle(sketch, "E20.16.18.0", {"center": v(-24.44, -574) * mm, "radius": 6.35 * mm});
            skCircle(sketch, "E20.16.19.0", {"center": v(-24.44, -612.1) * mm, "radius": 6.35 * mm});
            skCircle(sketch, "E20.17.0.0", {"center": v(13.66, 111.8) * mm, "radius": 6.35 * mm});
            skCircle(sketch, "E20.17.1.0", {"center": v(13.66, 73.7) * mm, "radius": 6.35 * mm});
            skCircle(sketch, "E20.17.2.0", {"center": v(13.66, 35.6) * mm, "radius": 6.35 * mm});
            skCircle(sketch, "E20.17.3.0", {"center": v(13.66, -2.5) * mm, "radius": 6.35 * mm});
            skCircle(sketch, "E20.17.4.0", {"center": v(13.66, -40.6) * mm, "radius": 6.35 * mm});
            skCircle(sketch, "E20.17.5.0", {"center": v(13.66, -78.7) * mm, "radius": 6.35 * mm});
            skCircle(sketch, "E20.17.6.0", {"center": v(13.66, -116.8) * mm, "radius": 6.35 * mm});
            skCircle(sketch, "E20.17.7.0", {"center": v(13.66, -154.9) * mm, "radius": 6.35 * mm});
            skCircle(sketch, "E20.17.8.0", {"center": v(13.66, -193) * mm, "radius": 6.35 * mm});
            skCircle(sketch, "E20.17.9.0", {"center": v(13.66, -231.1) * mm, "radius": 6.35 * mm});
            skCircle(sketch, "E20.17.10.0", {"center": v(13.66, -269.2) * mm, "radius": 6.35 * mm});
            skCircle(sketch, "E20.17.11.0", {"center": v(13.66, -307.3) * mm, "radius": 6.35 * mm});
            skCircle(sketch, "E20.17.12.0", {"center": v(13.66, -345.4) * mm, "radius": 6.35 * mm});
            skCircle(sketch, "E20.17.13.0", {"center": v(13.66, -383.5) * mm, "radius": 6.35 * mm});
            skCircle(sketch, "E20.17.14.0", {"center": v(13.66, -421.6) * mm, "radius": 6.35 * mm});
            skCircle(sketch, "E20.17.15.0", {"center": v(13.66, -459.7) * mm, "radius": 6.35 * mm});
            skCircle(sketch, "E20.17.16.0", {"center": v(13.66, -497.8) * mm, "radius": 6.35 * mm});
            skCircle(sketch, "E20.17.17.0", {"center": v(13.66, -535.9) * mm, "radius": 6.35 * mm});
            skCircle(sketch, "E20.17.18.0", {"center": v(13.66, -574) * mm, "radius": 6.35 * mm});
            skCircle(sketch, "E20.17.19.0", {"center": v(13.66, -612.1) * mm, "radius": 6.35 * mm});
            skLineSegment(sketch, "E20.direction1", {"start": v(-634.04, 111.8) * mm, "end": v(-595.94, 111.8) * mm, "construction": true});
            skLineSegment(sketch, "E20.direction2", {"start": v(-634.04, 111.8) * mm, "end": v(-634.04, 73.7) * mm, "construction": true});
            skSolve(sketch);
        }
        {
            var Q0;
            Q0 = qSketchRegion(id + "F8", true);
            extrude(context, id + "F9", {"entities" : qUnion([Q0]), "operationType" : NewBodyOperationType.REMOVE, "endBound" : BoundingType.THROUGH_ALL, "oppositeDirection" : true, "depth" : 25.4 * mm});
        }
        {
            var Q0;
            Q0=makeQuery(id+"F1.opExtrude","CAP_FACE",FACE,{"disambiguationData":[OSD([sQuery(id+"F0.wireOp",EDGE,"E0.rect.bottom"),sQuery(id+"F0.wireOp",EDGE,"E0.rect.top"),sQuery(id+"F0.wireOp",EDGE,"E0.rect.left"),sQuery(id+"F0.wireOp",EDGE,"E0.rect.right"),sQuery(id+"F0.wireOp",EDGE,"E1.0"),sQuery(id+"F0.wireOp",EDGE,"E2.0"),sQuery(id+"F0.wireOp",EDGE,"E3.0"),sQuery(id+"F0.wireOp",EDGE,"E4.0"),sQuery(id+"F0.wireOp",EDGE,"E5.trimOffspring"),sQuery(id+"F0.wireOp",EDGE,"E6.trimOffspring"),sQuery(id+"F0.wireOp",EDGE,"E7.trimOffspring"),sQuery(id+"F0.wireOp",EDGE,"E8.trimOffspring")])],"isStart":false});
            var sketch = newSketch(context, id + "F10", { "sketchPlane" : qUnion([Q0])});
            skLineSegment(sketch, "E21", {"start": v(0, 0) * mm, "end": v(0, 635) * mm});
            skLineSegment(sketch, "E22", {"start": v(0, 639.6) * mm, "end": v(0, -657.13) * mm});
            skLineSegment(sketch, "E23", {"start": v(0, -657.13) * mm, "end": v(1103.55, -657.13) * mm});
            skLineSegment(sketch, "E24", {"start": v(1103.55, -657.13) * mm, "end": v(1100.42, 698.34) * mm});
            skLineSegment(sketch, "E25", {"start": v(1100.42, 698.34) * mm, "end": v(11.35, 695.77) * mm});
            skLineSegment(sketch, "E26", {"start": v(11.35, 695.77) * mm, "end": v(-0.8, 635.62) * mm});
            skSolve(sketch);
        }
        {
            var Q0;
            Q0 = qSketchRegion(id + "F10", true);
            extrude(context, id + "F11", {"entities" : qUnion([Q0]), "endBound" : BoundingType.SYMMETRIC, "depth" : 25.4 * mm});
        }
        {
            var Q0;
            Q0=makeQuery(id+"F11.opExtrude","SWEPT_BODY",BODY,{"disambiguationData":[OSD([sQuery(id+"F10.wireOp",EDGE,"E22"),sQuery(id+"F10.wireOp",EDGE,"E23"),sQuery(id+"F10.wireOp",EDGE,"E24"),sQuery(id+"F10.wireOp",EDGE,"E25"),sQuery(id+"F10.wireOp",EDGE,"E26")])]});
            var Q1;
            Q1=makeQuery(id+"F1.opExtrude","SWEPT_BODY",BODY,{"disambiguationData":[OSD([sQuery(id+"F0.wireOp",EDGE,"E0.rect.bottom"),sQuery(id+"F0.wireOp",EDGE,"E0.rect.top"),sQuery(id+"F0.wireOp",EDGE,"E0.rect.left"),sQuery(id+"F0.wireOp",EDGE,"E0.rect.right"),sQuery(id+"F0.wireOp",EDGE,"E1.0"),sQuery(id+"F0.wireOp",EDGE,"E2.0"),sQuery(id+"F0.wireOp",EDGE,"E3.0"),sQuery(id+"F0.wireOp",EDGE,"E4.0"),sQuery(id+"F0.wireOp",EDGE,"E5.trimOffspring"),sQuery(id+"F0.wireOp",EDGE,"E6.trimOffspring"),sQuery(id+"F0.wireOp",EDGE,"E7.trimOffspring"),sQuery(id+"F0.wireOp",EDGE,"E8.trimOffspring")])]});
            booleanBodies(context, id + "F12", {"operationType" : BooleanOperationType.SUBTRACTION, "tools" : qUnion([Q0]), "targets" : qUnion([Q1])});
        }
        {
            var Q0;
            Q0=makeQuery(id+"F1.opExtrude","SWEPT_BODY",BODY,{"disambiguationData":[OSD([sQuery(id+"F0.wireOp",EDGE,"E0.rect.bottom"),sQuery(id+"F0.wireOp",EDGE,"E0.rect.top"),sQuery(id+"F0.wireOp",EDGE,"E0.rect.left"),sQuery(id+"F0.wireOp",EDGE,"E0.rect.right"),sQuery(id+"F0.wireOp",EDGE,"E1.0"),sQuery(id+"F0.wireOp",EDGE,"E2.0"),sQuery(id+"F0.wireOp",EDGE,"E3.0"),sQuery(id+"F0.wireOp",EDGE,"E4.0"),sQuery(id+"F0.wireOp",EDGE,"E5.trimOffspring"),sQuery(id+"F0.wireOp",EDGE,"E6.trimOffspring"),sQuery(id+"F0.wireOp",EDGE,"E7.trimOffspring"),sQuery(id+"F0.wireOp",EDGE,"E8.trimOffspring")])]});
            var Q1;
            Q1=qCreatedBy(makeId("Right.planeOp"),FACE);
            mirror(context, id + "F13", {"entities" : qUnion([Q0]), "mirrorPlane" : qUnion([Q1])});
        }
    });
